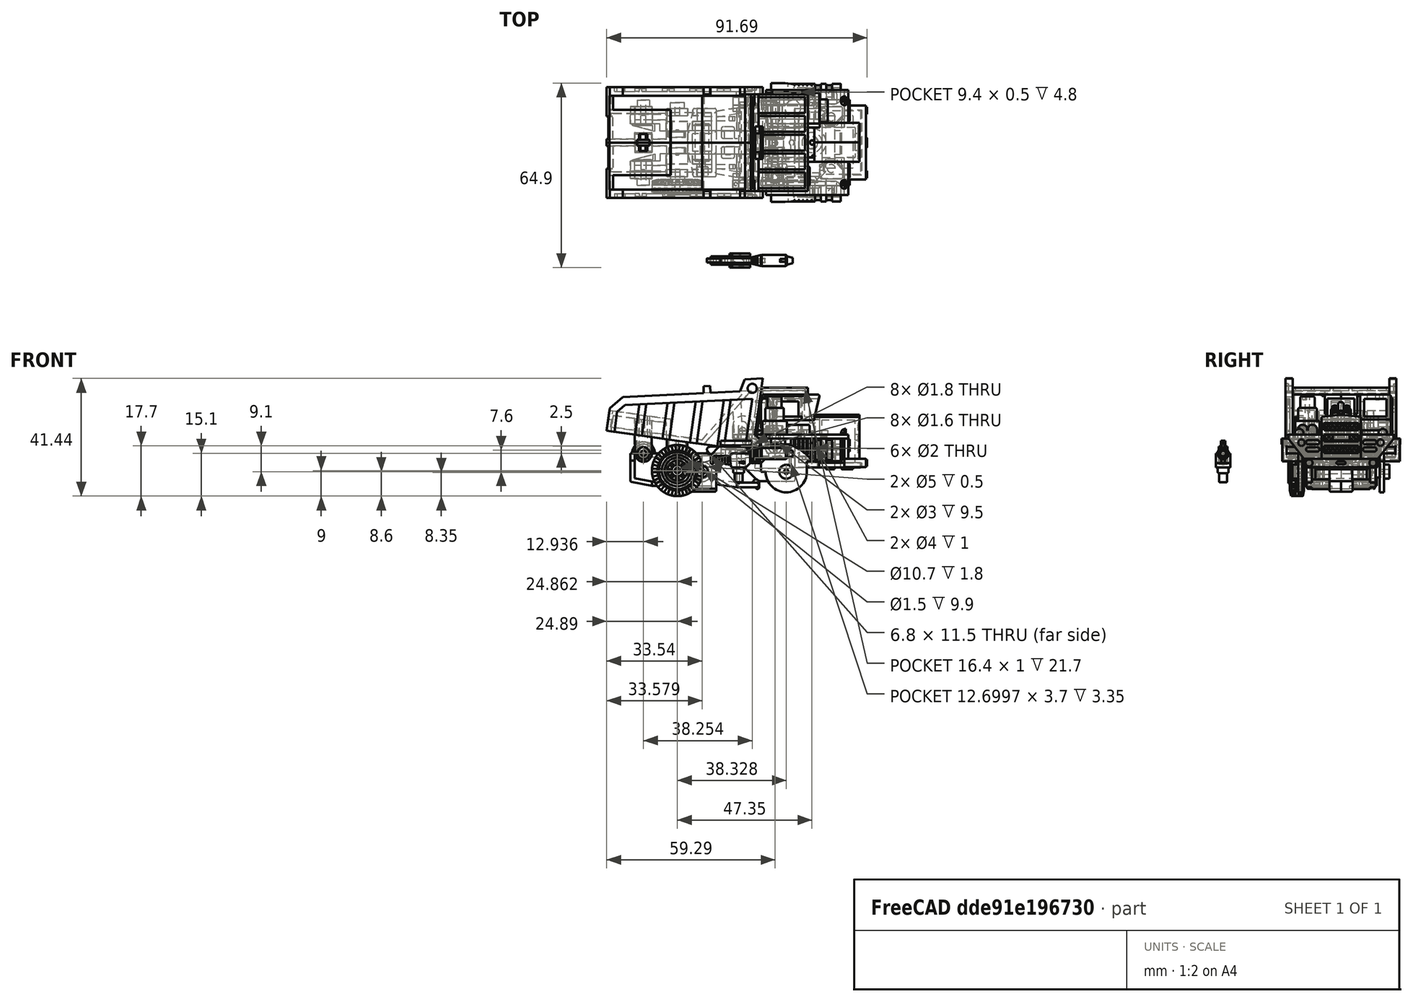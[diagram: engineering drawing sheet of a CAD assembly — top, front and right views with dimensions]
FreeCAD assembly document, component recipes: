
FREECAD ASSEMBLY — COMPONENT RECIPES ("Longhaul")

This assembly document has 21 components, labeled P0..P20 below (a component is one placed body or linked part). 19 of them carry a construction recipe — the FreeCAD feature program that regenerates the part from scratch, quoted from this document or its linked companion documents; the rest are supplied as boundary geometry only. No exploded tour is included for this assembly.
NOTE — this tour is split across 4 documents so each fits a 32k-token context. This is document 1: the component sections continue in the remaining 3 documents, each repeating the header above.
COMPONENT P0 — recipe-attached ("Lower_Torso", modeled in this document).
Construction recipe (the document's own serialized feature program — sketch geometry with constraints, then the solid features built on it; lengths are millimeters unless a unit is written):

FEATURE [Sketcher::SketchObject] Sketch
  ArcFitTolerance = 1e-06
  AttachmentSupport = -> [XY_Plane]
  FullyConstrained = true
  MakeInternals = false
  MapMode = 5
  sketch-geometry (8):
    g0: LineSegment StartX=0 StartY=11.25 StartZ=0 EndX=14.5 EndY=11.25 EndZ=0
    g1: LineSegment StartX=14.5 StartY=11.25 StartZ=0 EndX=14.5 EndY=-11.25 EndZ=0
    g2: LineSegment StartX=14.5 StartY=-11.25 StartZ=0 EndX=0 EndY=-11.25 EndZ=0
    g3: LineSegment StartX=0 StartY=-11.25 StartZ=0 EndX=0 EndY=-12 EndZ=0
    g4: LineSegment StartX=0 StartY=-12 StartZ=0 EndX=-8.5 EndY=-12 EndZ=0
    g5: LineSegment StartX=-8.5 StartY=-12 StartZ=0 EndX=-8.5 EndY=12 EndZ=0
    g6: LineSegment StartX=-8.5 StartY=12 StartZ=0 EndX=0 EndY=12 EndZ=0
    g7: LineSegment StartX=0 StartY=12 StartZ=0 EndX=0 EndY=11.25 EndZ=0
  constraints (26):
    c: Horizontal(g0)
    c: Coincident(g1,g0)
    c: Vertical(g1)
    c: Coincident(g2,g1)
    c: Horizontal(g2)
    c: Coincident(g3,g2)
    c: Vertical(g3)
    c: Coincident(g4,g3)
    c: Horizontal(g4)
    c: Coincident(g5,g4)
    c: Vertical(g5)
    c: Coincident(g6,g5)
    c: Horizontal(g6)
    c: Coincident(g7,g6)
    c: Coincident(g7,g0)
    c: Vertical(g7)
    c: DistanceY(g1,g1) = 22.5
    c: DistanceX(g0,g0) = 14.5
    c: DistanceX(g2,g2) = 14.5
    c: DistanceY(g3,g3) = 0.75
    c: DistanceY(g7,g7) = 0.75
    c: DistanceX(g6,g6) = 8.5
    c: DistanceY(g5,g5) = 24
    c: DistanceY(g-1,g5) = 12
    c: DistanceX(g5,g-1) = 8.5
    c: DistanceX(g5,g0) = 23
FEATURE [PartDesign::Pad] Pad
  Direction = (0,0,1)
  Length = 1.6
  Length2 = 10
  Profile = -> Sketch
  ReferenceAxis = -> Sketch [N_Axis]
  Refine = true
  Suppressed = false
  Type = 0
FEATURE [Sketcher::SketchObject] Sketch001
  ArcFitTolerance = 1e-06
  AttachmentSupport = -> [Pad]
  ExternalGeometry = -> [Pad]
  FullyConstrained = true
  MakeInternals = false
  MapMode = 5
  Placement = pos=(0,0,1.6) rot=(0,0,1;0rad)
  sketch-geometry (8):
    g0: LineSegment StartX=-8.5 StartY=12 StartZ=0 EndX=0 EndY=12 EndZ=0
    g1: LineSegment StartX=0 StartY=12 StartZ=0 EndX=0 EndY=10.6 EndZ=0
    g2: LineSegment StartX=0 StartY=10.6 StartZ=0 EndX=-7.1 EndY=10.6 EndZ=0
    g3: LineSegment StartX=-7.1 StartY=10.6 StartZ=0 EndX=-7.1 EndY=-10.6 EndZ=0
    g4: LineSegment StartX=-7.1 StartY=-10.6 StartZ=0 EndX=0 EndY=-10.6 EndZ=0
    g5: LineSegment StartX=0 StartY=-10.6 StartZ=0 EndX=0 EndY=-12 EndZ=0
    g6: LineSegment StartX=0 StartY=-12 StartZ=0 EndX=-8.5 EndY=-12 EndZ=0
    g7: LineSegment StartX=-8.5 StartY=-12 StartZ=0 EndX=-8.5 EndY=12 EndZ=0
  constraints (20):
    c: Coincident(g0,g-5)
    c: Coincident(g0,g-4)
    c: Coincident(g1,g0)
    c: PointOnObject(g1,g-2)
    c: Coincident(g2,g1)
    c: Horizontal(g2)
    c: Coincident(g3,g2)
    c: Vertical(g3)
    c: Coincident(g4,g3)
    c: PointOnObject(g4,g-2)
    c: Horizontal(g4)
    c: Coincident(g5,g4)
    c: Coincident(g5,g-7)
    c: Coincident(g6,g5)
    c: Coincident(g6,g-6)
    c: Coincident(g7,g6)
    c: Coincident(g7,g0)
    c: DistanceX(g6,g3) = 1.4
    c: DistanceY(g5,g4) = 1.4
    c: DistanceY(g2,g0) = 1.4
FEATURE [PartDesign::Pad] Pad001
  BaseFeature = -> Pad
  Direction = (0,0,1)
  Length = 8.5
  Length2 = 10
  Profile = -> Sketch001
  ReferenceAxis = -> Sketch001 [N_Axis]
  Refine = true
  Suppressed = false
  Type = 0
FEATURE [Sketcher::SketchObject] Sketch002
  ArcFitTolerance = 1e-06
  AttachmentSupport = -> [Pad001]
  ExternalGeometry = -> [Pad001]
  FullyConstrained = true
  MakeInternals = false
  MapMode = 5
  Placement = pos=(0,0,1.6) rot=(0,0,1;0rad)
  sketch-geometry (4):
    g0: LineSegment StartX=5.4 StartY=4.1 StartZ=0 EndX=5.4 EndY=-4.1 EndZ=0
    g1: LineSegment StartX=5.4 StartY=-4.1 StartZ=0 EndX=7.5 EndY=-4.1 EndZ=0
    g2: LineSegment StartX=7.5 StartY=-4.1 StartZ=0 EndX=7.5 EndY=4.1 EndZ=0
    g3: LineSegment StartX=7.5 StartY=4.1 StartZ=0 EndX=5.4 EndY=4.1 EndZ=0
  constraints (13):
    c: Coincident(g0,g1)
    c: Coincident(g1,g2)
    c: Coincident(g2,g3)
    c: Coincident(g3,g0)
    c: Vertical(g0)
    c: Vertical(g2)
    c: Horizontal(g1)
    c: Horizontal(g3)
    c: DistanceY(g2,g2) = 8.2
    c: DistanceX(g3,g3) = 2.1
    c: DistanceY(g-3,g-3) = 22.5
    c: DistanceY(g2,g-3) = 7.15
    c: DistanceX(g1,g-3) = 7
FEATURE [PartDesign::Pocket] Pocket
  BaseFeature = -> Pad001
  Direction = (0,0,-1)
  Length = 5
  Length2 = 5
  Profile = -> Sketch002
  ReferenceAxis = -> Sketch002 [N_Axis]
  Refine = true
  Suppressed = false
  Type = 0
FEATURE [Sketcher::SketchObject] Sketch003
  ArcFitTolerance = 1e-06
  AttachmentSupport = -> [Pocket]
  ExternalGeometry = -> [Pocket]
  FullyConstrained = true
  MakeInternals = false
  MapMode = 5
  Placement = pos=(0,0,10.1) rot=(0,0,1;0rad)
  sketch-geometry (4):
    g0: LineSegment StartX=-8.5 StartY=2.5 StartZ=0 EndX=-8.5 EndY=-2.5 EndZ=0
    g1: LineSegment StartX=-8.5 StartY=-2.5 StartZ=0 EndX=-7.1 EndY=-2.5 EndZ=0
    g2: LineSegment StartX=-7.1 StartY=-2.5 StartZ=0 EndX=-7.1 EndY=2.5 EndZ=0
    g3: LineSegment StartX=-7.1 StartY=2.5 StartZ=0 EndX=-8.5 EndY=2.5 EndZ=0
  constraints (12):
    c: Coincident(g0,g1)
    c: Coincident(g1,g2)
    c: Coincident(g2,g3)
    c: Coincident(g3,g0)
    c: Vertical(g0)
    c: Vertical(g2)
    c: Horizontal(g1)
    c: Horizontal(g3)
    c: PointOnObject(g0,g-4)
    c: PointOnObject(g1,g-3)
    c: DistanceY(g0,g0) = 5
    c: DistanceY(g1,g-1) = 2.5
FEATURE [PartDesign::Pocket] Pocket001
  BaseFeature = -> Pocket
  Direction = (0,0,-1)
  Length = 5
  Length2 = 5
  Profile = -> Sketch003
  ReferenceAxis = -> Sketch003 [N_Axis]
  Refine = true
  Suppressed = false
  Type = 0
FEATURE [Sketcher::SketchObject] Sketch004
  ArcFitTolerance = 1e-06
  AttachmentSupport = -> [Pocket001]
  ExternalGeometry = -> [Pocket001]
  FullyConstrained = true
  MakeInternals = false
  MapMode = 5
  Placement = pos=(0,0,10.1) rot=(0,0,1;0rad)
  sketch-geometry (4):
    g0: ArcOfCircle CenterX=-0.7 CenterY=-12 CenterZ=0 NormalX=0 NormalY=0 NormalZ=1 AngleXU=0 Radius=0.7 StartAngle=3.14159 EndAngle=6.28319
    g1: ArcOfCircle CenterX=-0.7 CenterY=12 CenterZ=0 NormalX=0 NormalY=0 NormalZ=1 AngleXU=0 Radius=0.7 StartAngle=-9e-16 EndAngle=3.14159
    g2: LineSegment StartX=0 StartY=-12 StartZ=0 EndX=-1.4 EndY=-12 EndZ=0
    g3: LineSegment StartX=0 StartY=12 StartZ=0 EndX=-1.4 EndY=12 EndZ=0
  constraints (13):
    c: Coincident(g0,g-3)
    c: PointOnObject(g0,g-3)
    c: Coincident(g1,g-4)
    c: PointOnObject(g1,g-4)
    c: PointOnObject(g0,g-3)
    c: PointOnObject(g1,g-4)
    c: DistanceY(g-5,g-5) = 1.4
    c: Radius(g1) = 0.7
    c: Radius(g0) = 0.7
    c: Coincident(g2,g0)
    c: Coincident(g2,g0)
    c: Coincident(g3,g1)
    c: Coincident(g3,g1)
FEATURE [PartDesign::Pad] Pad002
  BaseFeature = -> Pocket001
  Direction = (0,0,1)
  Length = 10
  Length2 = 10
  Profile = -> Sketch004
  ReferenceAxis = -> Sketch004 [N_Axis]
  Refine = true
  Reversed = true
  Suppressed = false
  Type = 0
FEATURE [Sketcher::SketchObject] Sketch005
  ArcFitTolerance = 1e-06
  AttachmentSupport = -> [Pad002]
  ExternalGeometry = -> [Pad002]
  FullyConstrained = true
  MakeInternals = false
  MapMode = 5
  Placement = pos=(0,-12,0) rot=(1,0,0;1.5708rad)
  sketch-geometry (8):
    g0: LineSegment StartX=0 StartY=10.1 StartZ=0 EndX=-2 EndY=10.1 EndZ=0
    g1: LineSegment StartX=-2 StartY=10.1 StartZ=0 EndX=-2 EndY=8.1 EndZ=0
    g2: LineSegment StartX=-2 StartY=8.1 StartZ=0 EndX=0 EndY=8.1 EndZ=0
    g3: LineSegment StartX=0 StartY=8.1 StartZ=0 EndX=0 EndY=10.1 EndZ=0
    g4: LineSegment StartX=0 StartY=0 StartZ=0 EndX=0 EndY=2 EndZ=0
    g5: LineSegment StartX=0 StartY=2 StartZ=0 EndX=-2 EndY=2 EndZ=0
    g6: LineSegment StartX=-2 StartY=2 StartZ=0 EndX=-2 EndY=0 EndZ=0
    g7: LineSegment StartX=-2 StartY=0 StartZ=0 EndX=0 EndY=0 EndZ=0
  constraints (22):
    c: Coincident(g0,g1)
    c: Coincident(g1,g2)
    c: Coincident(g2,g3)
    c: Coincident(g3,g0)
    c: Horizontal(g0)
    c: Horizontal(g2)
    c: Vertical(g1)
    c: Vertical(g3)
    c: Coincident(g0,g-5)
    c: Coincident(g4,g5)
    c: Coincident(g5,g6)
    c: Coincident(g6,g7)
    c: Coincident(g7,g4)
    c: Vertical(g4)
    c: Vertical(g6)
    c: Horizontal(g5)
    c: Horizontal(g7)
    c: Coincident(g4,g-1)
    c: DistanceY(g6,g6) = 2
    c: DistanceY(g1,g1) = 2
    c: DistanceX(g0,g0) = 2
    c: DistanceX(g5,g5) = 2
FEATURE [PartDesign::Pocket] Pocket002
  BaseFeature = -> Pad002
  Direction = (0,1,-2e-16)
  Length = 5
  Length2 = 5
  Profile = -> Sketch005
  ReferenceAxis = -> Sketch005 [N_Axis]
  Refine = true
  Reversed = true
  Suppressed = false
  Type = 0
FEATURE [Sketcher::SketchObject] Sketch006
  ArcFitTolerance = 1e-06
  AttachmentSupport = -> [Pocket002]
  ExternalGeometry = -> [Pocket002]
  FullyConstrained = true
  MakeInternals = false
  MapMode = 5
  Placement = pos=(0,12,0) rot=(0,0.707107,0.707107;3.14159rad)
  sketch-geometry (8):
    g0: LineSegment StartX=0 StartY=10.1 StartZ=0 EndX=0 EndY=8.1 EndZ=0
    g1: LineSegment StartX=0 StartY=8.1 StartZ=0 EndX=2 EndY=8.1 EndZ=0
    g2: LineSegment StartX=2 StartY=8.1 StartZ=0 EndX=2 EndY=10.1 EndZ=0
    g3: LineSegment StartX=2 StartY=10.1 StartZ=0 EndX=0 EndY=10.1 EndZ=0
    g4: LineSegment StartX=0 StartY=0 StartZ=0 EndX=2 EndY=0 EndZ=0
    g5: LineSegment StartX=2 StartY=0 StartZ=0 EndX=2 EndY=2 EndZ=0
    g6: LineSegment StartX=2 StartY=2 StartZ=0 EndX=0 EndY=2 EndZ=0
    g7: LineSegment StartX=0 StartY=2 StartZ=0 EndX=0 EndY=0 EndZ=0
  constraints (22):
    c: Coincident(g0,g1)
    c: Coincident(g1,g2)
    c: Coincident(g2,g3)
    c: Coincident(g3,g0)
    c: Vertical(g0)
    c: Vertical(g2)
    c: Horizontal(g1)
    c: Horizontal(g3)
    c: Coincident(g0,g-3)
    c: Coincident(g4,g5)
    c: Coincident(g5,g6)
    c: Coincident(g6,g7)
    c: Coincident(g7,g4)
    c: Horizontal(g4)
    c: Horizontal(g6)
    c: Vertical(g5)
    c: Vertical(g7)
    c: Coincident(g4,g-1)
    c: DistanceX(g6,g6) = 2
    c: DistanceX(g1,g1) = 2
    c: DistanceY(g2,g2) = 2
    c: DistanceY(g5,g5) = 2
FEATURE [PartDesign::Pocket] Pocket003
  BaseFeature = -> Pocket002
  Direction = (0,-1,2e-16)
  Length = 5
  Length2 = 5
  Profile = -> Sketch006
  ReferenceAxis = -> Sketch006 [N_Axis]
  Refine = true
  Reversed = true
  Suppressed = false
  Type = 0
FEATURE [Sketcher::SketchObject] Sketch007
  ArcFitTolerance = 1e-06
  AttachmentSupport = -> [Pocket003]
  ExternalGeometry = -> [Pocket003]
  FullyConstrained = true
  MakeInternals = false
  MapMode = 5
  Placement = pos=(0,0,0) rot=(1,0,0;3.14159rad)
  sketch-geometry (1):
    g0: Circle CenterX=-2.5 CenterY=0 CenterZ=0 NormalX=0 NormalY=0 NormalZ=1 AngleXU=0 Radius=1
  constraints (4):
    c: PointOnObject(g0,g-1)
    c: Radius(g0) = 1
    c: DistanceX(g0,g-3) = 17
    c: DistanceX(g-4,g0) = 6
FEATURE [PartDesign::Pocket] Pocket004
  BaseFeature = -> Pocket003
  Direction = (0,0,1)
  Length = 5
  Length2 = 5
  Profile = -> Sketch007
  ReferenceAxis = -> Sketch007 [N_Axis]
  Refine = true
  Suppressed = false
  Type = 0
FEATURE [Sketcher::SketchObject] Sketch008
  ArcFitTolerance = 1e-06
  AttachmentSupport = -> [Pocket004]
  ExternalGeometry = -> [Pocket004]
  FullyConstrained = false
  MakeInternals = false
  MapMode = 5
  Placement = pos=(0,0,1.6) rot=(0,0,1;0rad)
  sketch-geometry (1):
    g0: Circle CenterX=-2.5 CenterY=0 CenterZ=0 NormalX=0 NormalY=0 NormalZ=1 AngleXU=0 Radius=4.9
  constraints (1):
    c: Radius(g0) = 4.9
FEATURE [PartDesign::Pad] Pad003
  BaseFeature = -> Pocket004
  Direction = (0,0,1)
  Length = 1.2
  Length2 = 10
  Profile = -> Sketch008
  ReferenceAxis = -> Sketch008 [N_Axis]
  Refine = true
  Suppressed = false
  Type = 0
FEATURE [Sketcher::SketchObject] Sketch009
  ArcFitTolerance = 1e-06
  AttachmentSupport = -> [Pad003]
  ExternalGeometry = -> [Pad003]
  FullyConstrained = true
  MakeInternals = false
  MapMode = 5
  Placement = pos=(0,0,2.8) rot=(0,0,1;0rad)
  sketch-geometry (1):
    g0: Circle CenterX=-2.5 CenterY=0 CenterZ=0 NormalX=0 NormalY=0 NormalZ=1 AngleXU=0 Radius=3.55
  constraints (2):
    c: Coincident(g0,g-3)
    c: Radius(g0) = 3.55
FEATURE [PartDesign::Pad] Pad004
  BaseFeature = -> Pad003
  Direction = (0,0,1)
  Length = 1
  Length2 = 10
  Profile = -> Sketch009
  ReferenceAxis = -> Sketch009 [N_Axis]
  Refine = true
  Suppressed = false
  Type = 0
FEATURE [Sketcher::SketchObject] Sketch010
  ArcFitTolerance = 1e-06
  AttachmentSupport = -> [Pad004]
  ExternalGeometry = -> [Pad004]
  FullyConstrained = true
  MakeInternals = false
  MapMode = 5
  Placement = pos=(0,0,3.8) rot=(0,0,1;0rad)
  sketch-geometry (1):
    g0: Circle CenterX=-2.5 CenterY=0 CenterZ=0 NormalX=0 NormalY=0 NormalZ=1 AngleXU=0 Radius=2.25
  constraints (2):
    c: Coincident(g0,g-3)
    c: Diameter(g0) = 4.5
FEATURE [PartDesign::Pocket] Pocket005
  BaseFeature = -> Pad004
  Direction = (0,0,-1)
  Length = 1
  Length2 = 5
  Profile = -> Sketch010
  ReferenceAxis = -> Sketch010 [N_Axis]
  Refine = true
  Suppressed = false
  Type = 0
FEATURE [Sketcher::SketchObject] Sketch011
  ArcFitTolerance = 1e-06
  AttachmentSupport = -> [Pocket005]
  ExternalGeometry = -> [Pocket005]
  FullyConstrained = true
  MakeInternals = false
  MapMode = 5
  Placement = pos=(0,0,2.8) rot=(0,0,1;0rad)
  sketch-geometry (1):
    g0: Circle CenterX=-2.5 CenterY=0 CenterZ=0 NormalX=0 NormalY=0 NormalZ=1 AngleXU=0 Radius=1
  constraints (2):
    c: Coincident(g0,g-3)
    c: Radius(g0) = 1
FEATURE [PartDesign::Pocket] Pocket006
  BaseFeature = -> Pocket005
  Direction = (0,0,-1)
  Length = 1.2
  Length2 = 5
  Profile = -> Sketch011
  ReferenceAxis = -> Sketch011 [N_Axis]
  Refine = true
  Suppressed = false
  Type = 0
FEATURE [Sketcher::SketchObject] Sketch012
  ArcFitTolerance = 1e-06
  AttachmentSupport = -> [Pocket006]
  ExternalGeometry = -> [Sketch007]
  FullyConstrained = true
  MakeInternals = false
  MapMode = 5
  Placement = pos=(0,0,0) rot=(1,0,0;3.14159rad)
  sketch-geometry (1):
    g0: Circle CenterX=-2.5 CenterY=0 CenterZ=0 NormalX=0 NormalY=0 NormalZ=1 AngleXU=0 Radius=2
  constraints (2):
    c: Coincident(g0,g-3)
    c: Diameter(g0) = 4
FEATURE [PartDesign::Pocket] Pocket007
  BaseFeature = -> Pocket006
  Direction = (0,0,1)
  Length = 1.8
  Length2 = 5
  Profile = -> Sketch012
  ReferenceAxis = -> Sketch012 [N_Axis]
  Refine = true
  Suppressed = false
  Type = 0
FEATURE [Sketcher::SketchObject] Sketch013
  ArcFitTolerance = 1e-06
  AttachmentSupport = -> [Pocket007]
  ExternalGeometry = -> [Pocket007]
  FullyConstrained = true
  MakeInternals = false
  MapMode = 5
  Placement = pos=(0,0,0) rot=(1,0,0;3.14159rad)
  sketch-geometry (24):
    g0: LineSegment StartX=11.65 StartY=9 StartZ=0 EndX=8.15 EndY=9 EndZ=0
    g1: LineSegment StartX=7.9 StartY=8.75 StartZ=0 EndX=7.9 EndY=-9.25 EndZ=0
    g2: LineSegment StartX=8.15 StartY=-9.5 StartZ=0 EndX=11.65 EndY=-9.5 EndZ=0
    g3: LineSegment StartX=11.9 StartY=-9.25 StartZ=0 EndX=11.9 EndY=8.75 EndZ=0
    g4: LineSegment StartX=2.4 StartY=8.75 StartZ=0 EndX=2.4 EndY=-9.25 EndZ=0
    g5: LineSegment StartX=2.65 StartY=-9.5 StartZ=0 EndX=5.15 EndY=-9.5 EndZ=0
    g6: LineSegment StartX=5.4 StartY=-9.25 StartZ=0 EndX=5.4 EndY=8.75 EndZ=0
    g7: LineSegment StartX=5.15 StartY=9 StartZ=0 EndX=2.65 EndY=9 EndZ=0
    g8: ArcOfCircle CenterX=11.65 CenterY=8.75 CenterZ=0 NormalX=0 NormalY=0 NormalZ=1 AngleXU=0 Radius=0.25 StartAngle=2.7e-15 EndAngle=1.5708
    g9: GeomPoint [constr] X=11.9 Y=9 Z=0
    g10: ArcOfCircle CenterX=8.15 CenterY=8.75 CenterZ=0 NormalX=0 NormalY=0 NormalZ=1 AngleXU=0 Radius=0.25 StartAngle=1.5708 EndAngle=3.14159
    g11: GeomPoint [constr] X=7.9 Y=9 Z=0
    g12: ArcOfCircle CenterX=8.15 CenterY=-9.25 CenterZ=0 NormalX=0 NormalY=0 NormalZ=1 AngleXU=0 Radius=0.25 StartAngle=3.14159 EndAngle=4.71239
    g13: GeomPoint [constr] X=7.9 Y=-9.5 Z=0
    g14: ArcOfCircle CenterX=11.65 CenterY=-9.25 CenterZ=0 NormalX=0 NormalY=0 NormalZ=1 AngleXU=0 Radius=0.25 StartAngle=4.71239 EndAngle=6.28319
    g15: GeomPoint [constr] X=11.9 Y=-9.5 Z=0
    g16: ArcOfCircle CenterX=5.15 CenterY=-9.25 CenterZ=0 NormalX=0 NormalY=0 NormalZ=1 AngleXU=0 Radius=0.25 StartAngle=4.71239 EndAngle=6.28319
    g17: GeomPoint [constr] X=5.4 Y=-9.5 Z=0
    g18: ArcOfCircle CenterX=2.65 CenterY=-9.25 CenterZ=0 NormalX=0 NormalY=0 NormalZ=1 AngleXU=0 Radius=0.25 StartAngle=3.14159 EndAngle=4.71239
    g19: GeomPoint [constr] X=2.4 Y=-9.5 Z=0
    g20: ArcOfCircle CenterX=2.65 CenterY=8.75 CenterZ=0 NormalX=0 NormalY=0 NormalZ=1 AngleXU=0 Radius=0.25 StartAngle=1.5708 EndAngle=3.14159
    g21: GeomPoint [constr] X=2.4 Y=9 Z=0
    g22: ArcOfCircle CenterX=5.15 CenterY=8.75 CenterZ=0 NormalX=0 NormalY=0 NormalZ=1 AngleXU=0 Radius=0.25 StartAngle=2.9e-15 EndAngle=1.5708
    g23: GeomPoint [constr] X=5.4 Y=9 Z=0
  constraints (57):
    c: Horizontal(g0)
    c: Horizontal(g2)
    c: Vertical(g1)
    c: Vertical(g3)
    c: Vertical(g4)
    c: Vertical(g6)
    c: Horizontal(g5)
    c: Horizontal(g7)
    c: PointOnObject(g9,g0)
    c: PointOnObject(g9,g3)
    c: Tangent(g0,g8) = -1.5708
    c: Tangent(g3,g8) = -1.5708
    c: PointOnObject(g11,g0)
    c: PointOnObject(g11,g1)
    c: Tangent(g0,g10) = -1.5708
    c: Tangent(g1,g10) = -1.5708
    c: PointOnObject(g13,g1)
    c: PointOnObject(g13,g2)
    c: Tangent(g1,g12) = -1.5708
    c: Tangent(g2,g12) = -1.5708
    c: PointOnObject(g15,g2)
    c: PointOnObject(g15,g3)
    c: Tangent(g2,g14) = -1.5708
    c: Tangent(g3,g14) = -1.5708
    c: PointOnObject(g17,g5)
    c: PointOnObject(g17,g6)
    c: Tangent(g5,g16) = -1.5708
    c: Tangent(g6,g16) = -1.5708
    c: PointOnObject(g19,g4)
    c: PointOnObject(g19,g5)
    c: Tangent(g4,g18) = -1.5708
    c: Tangent(g5,g18) = -1.5708
    c: PointOnObject(g21,g4)
    c: PointOnObject(g21,g7)
    c: Tangent(g4,g20) = -1.5708
    c: Tangent(g7,g20) = -1.5708
    c: PointOnObject(g23,g6)
    c: PointOnObject(g23,g7)
    c: Tangent(g6,g22) = -1.5708
    c: Tangent(g7,g22) = -1.5708
    c: Radius(g20) = 0.25
    c: Radius(g22) = 0.25
    c: Radius(g18) = 0.25
    c: Radius(g16) = 0.25
    c: Radius(g12) = 0.25
    c: Radius(g14) = 0.25
    c: Radius(g10) = 0.25
    c: Radius(g8) = 0.25
    c: PointOnObject(g-3,g6)
    c: DistanceY(g3,g3) = 18
    c: DistanceY(g4,g4) = 18
    c: DistanceY(g-4,g-4) = 22.5
    c: DistanceY(g0,g-4) = 2.25
    c: DistanceY(g7,g-5) = 2.25
    c: DistanceX(g1,g3) = 4
    c: DistanceX(g4,g6) = 3
    c: DistanceX(g3,g-5) = 2.6
FEATURE [PartDesign::Pad] Pad005
  BaseFeature = -> Pocket007
  Direction = (0,0,-1)
  Length = 0.6
  Length2 = 10
  Profile = -> Sketch013
  ReferenceAxis = -> Sketch013 [N_Axis]
  Refine = true
  Suppressed = false
  Type = 0
FEATURE [Sketcher::SketchObject] Sketch014
  ArcFitTolerance = 1e-06
  AttachmentSupport = -> [Pad005]
  ExternalGeometry = -> [Pad005]
  FullyConstrained = true
  MakeInternals = false
  MapMode = 5
  Placement = pos=(-8.5,0,0) rot=(0.57735,-0.57735,-0.57735;2.0944rad)
  sketch-geometry (8):
    g0: LineSegment StartX=4 StartY=10.1 StartZ=0 EndX=4 EndY=3.4 EndZ=0
    g1: LineSegment StartX=4 StartY=3.4 StartZ=0 EndX=-4 EndY=3.4 EndZ=0
    g2: LineSegment StartX=-4 StartY=3.4 StartZ=0 EndX=-4 EndY=10.1 EndZ=0
    g3: LineSegment StartX=-4 StartY=10.1 StartZ=0 EndX=-2.5 EndY=10.1 EndZ=0
    g4: LineSegment StartX=2.5 StartY=10.1 StartZ=0 EndX=4 EndY=10.1 EndZ=0
    g5: LineSegment StartX=-2.5 StartY=10.1 StartZ=0 EndX=-2.5 EndY=5.1 EndZ=0
    g6: LineSegment StartX=-2.5 StartY=5.1 StartZ=0 EndX=2.5 EndY=5.1 EndZ=0
    g7: LineSegment StartX=2.5 StartY=5.1 StartZ=0 EndX=2.5 EndY=10.1 EndZ=0
  constraints (20):
    c: PointOnObject(g0,g-3)
    c: Vertical(g0)
    c: Coincident(g1,g0)
    c: Horizontal(g1)
    c: Coincident(g2,g1)
    c: PointOnObject(g2,g-7)
    c: Vertical(g2)
    c: Coincident(g3,g2)
    c: Coincident(g3,g-7)
    c: Coincident(g0,g4)
    c: Coincident(g5,g3)
    c: Coincident(g5,g-6)
    c: Coincident(g6,g5)
    c: Coincident(g6,g-5)
    c: Coincident(g7,g6)
    c: Coincident(g7,g4)
    c: DistanceX(g3,g3) = 1.5
    c: DistanceX(g4,g4) = 1.5
    c: DistanceY(g-8,g0) = 3.4
    c: Coincident(g4,g-4)
FEATURE [PartDesign::Pad] Pad006
  BaseFeature = -> Pad005
  Direction = (-1,0,0)
  Length = 17.6
  Length2 = 10
  Profile = -> Sketch014
  ReferenceAxis = -> Sketch014 [N_Axis]
  Refine = true
  Suppressed = false
  Type = 0
FEATURE [Sketcher::SketchObject] Sketch015
  ArcFitTolerance = 1e-06
  AttachmentSupport = -> [Pad006]
  ExternalGeometry = -> [Pad006]
  FullyConstrained = true
  MakeInternals = false
  MapMode = 5
  Placement = pos=(0,4,0) rot=(0,0.707107,0.707107;3.14159rad)
  sketch-geometry (8):
    g0: LineSegment StartX=11.9 StartY=10.1 StartZ=0 EndX=12.9 EndY=10.1 EndZ=0
    g1: LineSegment StartX=18.1 StartY=10.1 StartZ=0 EndX=19.1 EndY=10.1 EndZ=0
    g2: ArcOfCircle CenterX=15.5 CenterY=7.5 CenterZ=0 NormalX=0 NormalY=0 NormalZ=1 AngleXU=0 Radius=3.6 StartAngle=3.14159 EndAngle=6.28319
    g3: LineSegment StartX=11.9 StartY=10.1 StartZ=0 EndX=11.9 EndY=7.5 EndZ=0
    g4: LineSegment StartX=19.1 StartY=7.5 StartZ=0 EndX=19.1 EndY=10.1 EndZ=0
    g5: ArcOfCircle CenterX=15.5 CenterY=7.5 CenterZ=0 NormalX=0 NormalY=0 NormalZ=1 AngleXU=0 Radius=2.6 StartAngle=3.14159 EndAngle=6.28319
    g6: LineSegment StartX=18.1 StartY=7.5 StartZ=0 EndX=18.1 EndY=10.1 EndZ=0
    g7: LineSegment StartX=12.9 StartY=7.5 StartZ=0 EndX=12.9 EndY=10.1 EndZ=0
  constraints (25):
    c: PointOnObject(g0,g-4)
    c: PointOnObject(g0,g-4)
    c: PointOnObject(g1,g-4)
    c: DistanceX(g-4,g0) = 3.4
    c: DistanceX(g0,g0) = 1
    c: DistanceX(g1,g1) = 1
    c: DistanceX(g0,g1) = 5.2
    c: Diameter(g2) = 7.2
    c: Coincident(g3,g0)
    c: Coincident(g3,g2)
    c: Coincident(g4,g2)
    c: Coincident(g4,g1)
    c: Vertical(g4)
    c: Vertical(g3)
    c: DistanceY(g2,g2) = 0
    c: PointOnObject(g1,g-4)
    c: Diameter(g5) = 5.2
    c: Coincident(g6,g5)
    c: Coincident(g6,g1)
    c: Vertical(g6)
    c: Coincident(g7,g5)
    c: Coincident(g7,g0)
    c: Vertical(g7)
    c: Coincident(g5,g2)
    c: DistanceY(g-5,g2) = 4.1
FEATURE [PartDesign::Pad] Pad007
  BaseFeature = -> Pad006
  Direction = (0,1,-2e-16)
  Length = 9
  Length2 = 10
  Profile = -> Sketch015
  ReferenceAxis = -> Sketch015 [N_Axis]
  Refine = true
  Suppressed = false
  Type = 0
FEATURE [Sketcher::SketchObject] Sketch016
  ArcFitTolerance = 1e-06
  AttachmentSupport = -> [Pad007]
  ExternalGeometry = -> [Pad007]
  FullyConstrained = true
  MakeInternals = false
  MapMode = 5
  Placement = pos=(0,-4,0) rot=(1,0,0;1.5708rad)
  sketch-geometry (8):
    g0: LineSegment StartX=-11.9 StartY=10.1 StartZ=0 EndX=-12.9 EndY=10.1 EndZ=0
    g1: LineSegment StartX=-18.1 StartY=10.1 StartZ=0 EndX=-19.1 EndY=10.1 EndZ=0
    g2: ArcOfCircle CenterX=-15.5 CenterY=7.5 CenterZ=0 NormalX=0 NormalY=0 NormalZ=1 AngleXU=0 Radius=3.6 StartAngle=3.14159 EndAngle=6.28319
    g3: LineSegment StartX=-11.9 StartY=10.1 StartZ=0 EndX=-11.9 EndY=7.5 EndZ=0
    g4: LineSegment StartX=-19.1 StartY=10.1 StartZ=0 EndX=-19.1 EndY=7.5 EndZ=0
    g5: ArcOfCircle CenterX=-15.5 CenterY=7.5 CenterZ=0 NormalX=0 NormalY=0 NormalZ=1 AngleXU=0 Radius=2.6 StartAngle=3.14159 EndAngle=6.28319
    g6: LineSegment StartX=-18.1 StartY=10.1 StartZ=0 EndX=-18.1 EndY=7.5 EndZ=0
    g7: LineSegment StartX=-12.9 StartY=10.1 StartZ=0 EndX=-12.9 EndY=7.5 EndZ=0
  constraints (25):
    c: PointOnObject(g0,g-3)
    c: PointOnObject(g0,g-3)
    c: PointOnObject(g1,g-3)
    c: PointOnObject(g1,g-3)
    c: DistanceX(g0,g-3) = 3.4
    c: DistanceX(g0,g0) = 1
    c: DistanceX(g1,g1) = 1
    c: DistanceX(g1,g0) = 5.2
    c: Diameter(g2) = 7.2
    c: Coincident(g3,g0)
    c: Coincident(g3,g2)
    c: Coincident(g4,g1)
    c: Coincident(g4,g2)
    c: Vertical(g4)
    c: Vertical(g3)
    c: Coincident(g6,g1)
    c: Coincident(g6,g5)
    c: Vertical(g6)
    c: Coincident(g7,g0)
    c: Coincident(g7,g5)
    c: Coincident(g2,g5)
    c: Diameter(g5) = 5.2
    c: DistanceY(g-4,g2) = 4.1
    c: Vertical(g7)
    c: DistanceY(g5,g2) = 0
FEATURE [PartDesign::Pad] Pad008
  BaseFeature = -> Pad007
  Direction = (0,-1,2e-16)
  Length = 9
  Length2 = 10
  Profile = -> Sketch016
  ReferenceAxis = -> Sketch016 [N_Axis]
  Refine = true
  Suppressed = false
  Type = 0
FEATURE [Sketcher::SketchObject] Sketch017
  ArcFitTolerance = 1e-06
  AttachmentSupport = -> [Pad008]
  ExternalGeometry = -> [Pad008]
  FullyConstrained = false
  MakeInternals = false
  MapMode = 5
  Placement = pos=(0,4,0) rot=(0,0.707107,0.707107;3.14159rad)
  sketch-geometry (4):
    g0: LineSegment StartX=12.9 StartY=10.1 StartZ=0 EndX=12.9 EndY=7.5 EndZ=0
    g1: LineSegment StartX=12.9 StartY=10.1 StartZ=0 EndX=18.1 EndY=10.1 EndZ=0
    g2: LineSegment StartX=18.1 StartY=10.1 StartZ=0 EndX=18.1 EndY=7.5 EndZ=0
    g3: ArcOfCircle CenterX=15.5 CenterY=7.5 CenterZ=0 NormalX=0 NormalY=0 NormalZ=1 AngleXU=0 Radius=2.6 StartAngle=3.14159 EndAngle=6.28319
  constraints (8):
    c: Coincident(g0,g-3)
    c: Coincident(g0,g-4)
    c: Coincident(g1,g0)
    c: Coincident(g1,g-3)
    c: Coincident(g2,g1)
    c: Coincident(g2,g-4)
    c: Coincident(g3,g2)
    c: Coincident(g3,g0)
FEATURE [PartDesign::Pocket] Pocket008
  BaseFeature = -> Pad008
  Direction = (0,-1,2e-16)
  Length = 1.5
  Length2 = 5
  Profile = -> Sketch017
  ReferenceAxis = -> Sketch017 [N_Axis]
  Refine = true
  Suppressed = false
  Type = 0
FEATURE [Sketcher::SketchObject] Sketch018
  ArcFitTolerance = 1e-06
  AttachmentSupport = -> [Pocket008]
  ExternalGeometry = -> [Pocket008]
  FullyConstrained = true
  MakeInternals = false
  MapMode = 5
  Placement = pos=(0,-4,0) rot=(1,0,0;1.5708rad)
  sketch-geometry (4):
    g0: LineSegment StartX=-18.1 StartY=7.5 StartZ=0 EndX=-18.1 EndY=10.1 EndZ=0
    g1: LineSegment StartX=-18.1 StartY=10.1 StartZ=0 EndX=-12.9 EndY=10.1 EndZ=0
    g2: LineSegment StartX=-12.9 StartY=10.1 StartZ=0 EndX=-12.9 EndY=7.5 EndZ=0
    g3: ArcOfCircle CenterX=-15.5 CenterY=7.5 CenterZ=0 NormalX=0 NormalY=0 NormalZ=1 AngleXU=0 Radius=2.6 StartAngle=3.14159 EndAngle=6.28319
  constraints (8):
    c: Coincident(g0,g-5)
    c: Coincident(g0,g-4)
    c: Coincident(g1,g0)
    c: Coincident(g1,g-3)
    c: Coincident(g2,g1)
    c: Coincident(g2,g-5)
    c: Coincident(g3,g2)
    c: Tangent(g3,g-5) = -1.5708
FEATURE [PartDesign::Pocket] Pocket009
  BaseFeature = -> Pocket008
  Direction = (0,1,-2e-16)
  Length = 1.5
  Length2 = 5
  Profile = -> Sketch018
  ReferenceAxis = -> Sketch018 [N_Axis]
  Refine = true
  Suppressed = false
  Type = 0
FEATURE [Sketcher::SketchObject] Sketch019
  ArcFitTolerance = 1e-06
  AttachmentSupport = -> [Pocket009]
  ExternalGeometry = -> [Pocket009]
  FullyConstrained = true
  MakeInternals = false
  MapMode = 5
  Placement = pos=(0,2.5,0) rot=(1,0,0;1.5708rad)
  sketch-geometry (8):
    g0: LineSegment StartX=-18.75 StartY=10.1 StartZ=0 EndX=-17 EndY=10.1 EndZ=0
    g1: LineSegment StartX=-12.25 StartY=10.1 StartZ=0 EndX=-14 EndY=10.1 EndZ=0
    g2: LineSegment StartX=-14 StartY=10.1 StartZ=0 EndX=-14 EndY=6.9 EndZ=0
    g3: LineSegment StartX=-17 StartY=10.1 StartZ=0 EndX=-17 EndY=6.9 EndZ=0
    g4: ArcOfCircle CenterX=-15.5 CenterY=6.9 CenterZ=0 NormalX=0 NormalY=0 NormalZ=1 AngleXU=0 Radius=1.5 StartAngle=3.14159 EndAngle=6.28319
    g5: LineSegment StartX=-18.75 StartY=10.1 StartZ=0 EndX=-18.75 EndY=5.1 EndZ=0
    g6: LineSegment StartX=-18.75 StartY=5.1 StartZ=0 EndX=-12.25 EndY=5.1 EndZ=0
    g7: LineSegment StartX=-12.25 StartY=10.1 StartZ=0 EndX=-12.25 EndY=5.1 EndZ=0
  constraints (25):
    c: PointOnObject(g0,g-9)
    c: Horizontal(g0)
    c: PointOnObject(g1,g-3)
    c: Horizontal(g1)
    c: Coincident(g2,g1)
    c: Vertical(g2)
    c: Coincident(g3,g0)
    c: Vertical(g3)
    c: Coincident(g4,g3)
    c: Coincident(g4,g2)
    c: Coincident(g5,g0)
    c: PointOnObject(g5,g-10)
    c: Vertical(g5)
    c: PointOnObject(g6,g-6)
    c: Coincident(g7,g6)
    c: Vertical(g7)
    c: Coincident(g7,g1)
    c: Coincident(g6,g5)
    c: DistanceX(g0,g1) = 3
    c: DistanceX(g0,g0) = 1.75
    c: DistanceX(g1,g1) = 1.75
    c: DistanceY(g4,g3) = 0
    c: DistanceY(g4,g2) = 0
    c: DistanceX(g-7,g4) = 0
    c: DistanceY(g4,g-7) = 0.6
FEATURE [PartDesign::Pad] Pad009
  BaseFeature = -> Pocket009
  Direction = (0,-1,2e-16)
  Length = 0.8
  Length2 = 10
  Profile = -> Sketch019
  ReferenceAxis = -> Sketch019 [N_Axis]
  Refine = true
  Suppressed = false
  Type = 0
FEATURE [Sketcher::SketchObject] Sketch020
  ArcFitTolerance = 1e-06
  AttachmentSupport = -> [Pad009]
  ExternalGeometry = -> [Pad009]
  FullyConstrained = true
  MakeInternals = false
  MapMode = 5
  Placement = pos=(0,-2.5,0) rot=(0,0.707107,0.707107;3.14159rad)
  sketch-geometry (8):
    g0: LineSegment StartX=12.25 StartY=10.1 StartZ=0 EndX=14 EndY=10.1 EndZ=0
    g1: LineSegment StartX=18.75 StartY=10.1 StartZ=0 EndX=17 EndY=10.1 EndZ=0
    g2: LineSegment StartX=17 StartY=10.1 StartZ=0 EndX=17 EndY=6.9 EndZ=0
    g3: LineSegment StartX=14 StartY=10.1 StartZ=0 EndX=14 EndY=6.9 EndZ=0
    g4: ArcOfCircle CenterX=15.5 CenterY=6.9 CenterZ=0 NormalX=0 NormalY=0 NormalZ=1 AngleXU=0 Radius=1.5 StartAngle=3.14159 EndAngle=6.28319
    g5: LineSegment StartX=12.25 StartY=10.1 StartZ=0 EndX=12.25 EndY=5.1 EndZ=0
    g6: LineSegment StartX=18.75 StartY=10.1 StartZ=0 EndX=18.75 EndY=5.1 EndZ=0
    g7: LineSegment StartX=18.75 StartY=5.1 StartZ=0 EndX=12.25 EndY=5.1 EndZ=0
  constraints (25):
    c: PointOnObject(g0,g-3)
    c: Horizontal(g0)
    c: PointOnObject(g1,g-8)
    c: Horizontal(g1)
    c: Coincident(g2,g1)
    c: Vertical(g2)
    c: Coincident(g3,g0)
    c: Vertical(g3)
    c: Coincident(g4,g3)
    c: Coincident(g4,g2)
    c: Coincident(g5,g0)
    c: PointOnObject(g5,g-10)
    c: Vertical(g5)
    c: Coincident(g6,g1)
    c: PointOnObject(g6,g-9)
    c: Vertical(g6)
    c: Coincident(g7,g6)
    c: Coincident(g7,g5)
    c: DistanceX(g0,g1) = 3
    c: DistanceX(g0,g0) = 1.75
    c: DistanceX(g1,g1) = 1.75
    c: DistanceX(g-6,g4) = 0
    c: DistanceY(g4,g-6) = 0.6
    c: DistanceY(g4,g2) = 0
    c: DistanceY(g4,g3) = 0
FEATURE [PartDesign::Pad] Pad010
  BaseFeature = -> Pad009
  Direction = (0,1,-2e-16)
  Length = 0.8
  Length2 = 10
  Profile = -> Sketch020
  ReferenceAxis = -> Sketch020 [N_Axis]
  Refine = true
  Suppressed = false
  Type = 0
FEATURE [Sketcher::SketchObject] Sketch021
  ArcFitTolerance = 1e-06
  AttachmentSupport = -> [Pad010]
  ExternalGeometry = -> [Pad010]
  FullyConstrained = true
  MakeInternals = false
  MapMode = 5
  Placement = pos=(0,4,0) rot=(0,0.707107,0.707107;3.14159rad)
  sketch-geometry (8):
    g0: LineSegment StartX=26.1 StartY=10.1 StartZ=0 EndX=25 EndY=10.1 EndZ=0
    g1: LineSegment StartX=26.1 StartY=10.1 StartZ=0 EndX=26.1 EndY=7.49999 EndZ=0
    g2: LineSegment StartX=22.2 StartY=10.1 StartZ=0 EndX=21.1 EndY=10.1 EndZ=0
    g3: LineSegment StartX=22.2 StartY=10.1 StartZ=0 EndX=22.2 EndY=7.5 EndZ=0
    g4: LineSegment StartX=25 StartY=10.1 StartZ=0 EndX=25 EndY=7.5 EndZ=0
    g5: LineSegment StartX=21.1 StartY=10.1 StartZ=0 EndX=21.1 EndY=7.5 EndZ=0
    g6: ArcOfCircle CenterX=23.6 CenterY=7.5 CenterZ=0 NormalX=0 NormalY=0 NormalZ=1 AngleXU=0 Radius=1.4 StartAngle=3.14159 EndAngle=6.28319
    g7: ArcOfCircle CenterX=23.6 CenterY=7.5 CenterZ=0 NormalX=0 NormalY=0 NormalZ=1 AngleXU=0 Radius=2.5 StartAngle=3.14159 EndAngle=6.28318
  constraints (24):
    c: Coincident(g0,g-4)
    c: PointOnObject(g0,g-3)
    c: Coincident(g1,g0)
    c: PointOnObject(g1,g-4)
    c: PointOnObject(g2,g-3)
    c: PointOnObject(g2,g-3)
    c: Coincident(g3,g2)
    c: Vertical(g3)
    c: Coincident(g4,g0)
    c: Vertical(g4)
    c: Coincident(g5,g2)
    c: Vertical(g5)
    c: Coincident(g6,g4)
    c: Coincident(g6,g3)
    c: Coincident(g7,g1)
    c: Coincident(g7,g5)
    c: DistanceX(g0,g0) = 1.1
    c: DistanceX(g2,g2) = 1.1
    c: Coincident(g6,g7)
    c: DistanceX(g2,g0) = 5
    c: DistanceY(g3,g6) = 0
    c: DistanceY(g4,g6) = 0
    c: DistanceY(g6,g5) = 0
    c: DistanceY(g-4,g6) = 4.1
FEATURE [PartDesign::Pad] Pad011
  BaseFeature = -> Pad010
  Direction = (0,1,-2e-16)
  Length = 3.1
  Length2 = 10
  Profile = -> Sketch021
  ReferenceAxis = -> Sketch021 [N_Axis]
  Refine = true
  Suppressed = false
  Type = 0
FEATURE [PartDesign::Body] Body  label="Lower_Torso"
  AllowCompound = false
  Group = -> [Sketch,Pad,Sketch001,Pad001,Sketch002,Pocket,Sketch003,Pocket001,Sketch004,Pad002,Sketch005,Pocket002,Sketch006,Pocket003,Sketch007,Pocket004,Sketch008,Pad003,Sketch009,Pad004,Sketch010,Pocket005,Sketch011,Pocket006,Sketch012,Pocket007,Sketch013,Pad005,Sketch014,Pad006,Sketch015,Pad007,Sketch016,Pad008,Sketch017,Pocket008,Sketch018,Pocket009,Sketch019,Pad009,Sketch020,Pad010,Sketch021,Pad011,+77 more]
  Origin = -> Origin
  Tip = -> Pad243
COMPONENT P1 — recipe-attached ("Upper_Torso", modeled in this document).
Construction recipe (the document's own serialized feature program — sketch geometry with constraints, then the solid features built on it; lengths are millimeters unless a unit is written):

FEATURE [PartDesign::SubShapeBinder] Binder
  BindCopyOnChange = 0
  BindMode = 2
  ClaimChildren = false
  Context = -> Body001 [Binder.]
  Fuse = false
  MakeFace = true
  OffsetFill = false
  OffsetIntersection = false
  OffsetJoinType = 0
  OffsetOpenResult = false
  PartialLoad = false
  Refine = true
  Relative = true
  _Version = 2
FEATURE [Sketcher::SketchObject] Sketch039
  ArcFitTolerance = 1e-06
  AttachmentSupport = -> [Binder]
  FullyConstrained = true
  MakeInternals = false
  MapMode = 5
  Placement = pos=(0,0,10.1) rot=(0,0,1;0rad)
  sketch-geometry (12):
    g0: LineSegment StartX=10.3 StartY=18.5 StartZ=0 EndX=-18.7 EndY=18.5 EndZ=0
    g1: LineSegment StartX=-18.7 StartY=18.5 StartZ=0 EndX=-18.7 EndY=16 EndZ=0
    g2: LineSegment StartX=-18.7 StartY=16 StartZ=0 EndX=-30.4 EndY=16 EndZ=0
    g3: LineSegment StartX=-30.4 StartY=16 StartZ=0 EndX=-30.4 EndY=11 EndZ=0
    g4: LineSegment StartX=-30.4 StartY=11 StartZ=0 EndX=-27.5 EndY=11 EndZ=0
    g5: LineSegment StartX=-27.5 StartY=11 StartZ=0 EndX=-27.5 EndY=-11 EndZ=0
    g6: LineSegment StartX=-27.5 StartY=-11 StartZ=0 EndX=-30.4 EndY=-11 EndZ=0
    g7: LineSegment StartX=-30.4 StartY=-11 StartZ=0 EndX=-30.4 EndY=-16 EndZ=0
    g8: LineSegment StartX=-30.4 StartY=-16 StartZ=0 EndX=-18.7 EndY=-16 EndZ=0
    g9: LineSegment StartX=-18.7 StartY=-16 StartZ=0 EndX=-18.7 EndY=-18.5 EndZ=0
    g10: LineSegment StartX=-18.7 StartY=-18.5 StartZ=0 EndX=10.3 EndY=-18.5 EndZ=0
    g11: LineSegment StartX=10.3 StartY=-18.5 StartZ=0 EndX=10.3 EndY=18.5 EndZ=0
  constraints (38):
    c: Horizontal(g0)
    c: Coincident(g1,g0)
    c: Vertical(g1)
    c: Coincident(g2,g1)
    c: Horizontal(g2)
    c: Coincident(g3,g2)
    c: Vertical(g3)
    c: Coincident(g4,g3)
    c: Horizontal(g4)
    c: Coincident(g5,g4)
    c: Vertical(g5)
    c: Coincident(g6,g5)
    c: Horizontal(g6)
    c: Coincident(g7,g6)
    c: Vertical(g7)
    c: Coincident(g8,g7)
    c: Horizontal(g8)
    c: Coincident(g9,g8)
    c: Vertical(g9)
    c: Coincident(g10,g9)
    c: Horizontal(g10)
    c: Coincident(g11,g10)
    c: Coincident(g11,g0)
    c: Vertical(g11)
    c: DistanceY(g11,g11) = 37
    c: DistanceX(g0,g0) = 29
    c: DistanceX(g10,g10) = 29
    c: DistanceY(g7,g7) = 5
    c: DistanceY(g3,g3) = 5
    c: DistanceY(g5,g5) = 22
    c: DistanceY(g1,g1) = 2.5
    c: DistanceY(g9,g9) = 2.5
    c: DistanceX(g8,g8) = 11.7
    c: DistanceX(g2,g2) = 11.7
    c: DistanceX(g4,g4) = 2.9
    c: DistanceX(g7,g10) = 40.7
    c: DistanceY(g-1,g0) = 18.5
    c: DistanceX(g4,g-1) = 27.5
FEATURE [PartDesign::Pad] Pad021
  Direction = (0,0,1)
  Length = 1.5
  Length2 = 10
  Profile = -> Sketch039
  ReferenceAxis = -> Sketch039 [N_Axis]
  Refine = true
  Suppressed = false
  Type = 0
FEATURE [Sketcher::SketchObject] Sketch040
  ArcFitTolerance = 1e-06
  AttachmentSupport = -> [Pad021]
  ExternalGeometry = -> [Pad021]
  FullyConstrained = true
  MakeInternals = false
  MapMode = 5
  Placement = pos=(0,0,11.6) rot=(0,0,1;0rad)
  sketch-geometry (4):
    g0: LineSegment StartX=-24.75 StartY=2.5 StartZ=0 EndX=-24.75 EndY=-2.5 EndZ=0
    g1: LineSegment StartX=-24.75 StartY=-2.5 StartZ=0 EndX=-20.35 EndY=-2.5 EndZ=0
    g2: LineSegment StartX=-20.35 StartY=-2.5 StartZ=0 EndX=-20.35 EndY=2.5 EndZ=0
    g3: LineSegment StartX=-20.35 StartY=2.5 StartZ=0 EndX=-24.75 EndY=2.5 EndZ=0
  constraints (12):
    c: Coincident(g0,g1)
    c: Coincident(g1,g2)
    c: Coincident(g2,g3)
    c: Coincident(g3,g0)
    c: Vertical(g0)
    c: Vertical(g2)
    c: Horizontal(g1)
    c: Horizontal(g3)
    c: DistanceX(g3,g3) = 4.4
    c: DistanceY(g2,g2) = 5
    c: DistanceY(g-1,g2) = 2.5
    c: DistanceX(g-3,g0) = 2.75
FEATURE [PartDesign::Pocket] Pocket021
  BaseFeature = -> Pad021
  Direction = (0,0,-1)
  Length = 5
  Length2 = 5
  Profile = -> Sketch040
  ReferenceAxis = -> Sketch040 [N_Axis]
  Refine = true
  Suppressed = false
  Type = 0
FEATURE [Sketcher::SketchObject] Sketch043
  ArcFitTolerance = 1e-06
  AttachmentSupport = -> [Pocket021]
  ExternalGeometry = -> [Pocket021]
  FullyConstrained = true
  MakeInternals = false
  MapMode = 5
  Placement = pos=(0,0,11.6) rot=(0,0,1;0rad)
  sketch-geometry (4):
    g0: LineSegment StartX=10.3 StartY=5.3 StartZ=0 EndX=-12.65 EndY=5.3 EndZ=0
    g1: LineSegment StartX=-12.65 StartY=5.3 StartZ=0 EndX=-12.65 EndY=-5.3 EndZ=0
    g2: LineSegment StartX=-12.65 StartY=-5.3 StartZ=0 EndX=10.3 EndY=-5.3 EndZ=0
    g3: LineSegment StartX=10.3 StartY=-5.3 StartZ=0 EndX=10.3 EndY=5.3 EndZ=0
  constraints (12):
    c: Coincident(g0,g1)
    c: Coincident(g1,g2)
    c: Coincident(g2,g3)
    c: Coincident(g3,g0)
    c: Horizontal(g0)
    c: Horizontal(g2)
    c: Vertical(g1)
    c: Vertical(g3)
    c: PointOnObject(g0,g-3)
    c: DistanceY(g1,g1) = 10.6
    c: DistanceY(g-1,g0) = 5.3
    c: DistanceX(g-4,g0) = 7.7
FEATURE [PartDesign::Pocket] Pocket022
  BaseFeature = -> Pocket021
  Direction = (0,0,-1)
  Length = 5
  Length2 = 5
  Profile = -> Sketch043
  ReferenceAxis = -> Sketch043 [N_Axis]
  Refine = true
  Suppressed = false
  Type = 0
FEATURE [Sketcher::SketchObject] Sketch044
  ArcFitTolerance = 1e-06
  AttachmentSupport = -> [Pocket022]
  ExternalGeometry = -> [Pocket022]
  FullyConstrained = true
  MakeInternals = false
  MapMode = 5
  Placement = pos=(0,0,11.6) rot=(0,0,1;0rad)
  sketch-geometry (8):
    g0: LineSegment StartX=-28.4 StartY=-16 StartZ=0 EndX=-25.3 EndY=-16 EndZ=0
    g1: LineSegment StartX=-25.3 StartY=-16 StartZ=0 EndX=-25.3 EndY=-12.5 EndZ=0
    g2: LineSegment StartX=-25.3 StartY=-12.5 StartZ=0 EndX=-28.4 EndY=-12.5 EndZ=0
    g3: LineSegment StartX=-28.4 StartY=-12.5 StartZ=0 EndX=-28.4 EndY=-16 EndZ=0
    g4: LineSegment StartX=-28.4 StartY=16 StartZ=0 EndX=-28.4 EndY=12.5 EndZ=0
    g5: LineSegment StartX=-28.4 StartY=12.5 StartZ=0 EndX=-25.3 EndY=12.5 EndZ=0
    g6: LineSegment StartX=-25.3 StartY=12.5 StartZ=0 EndX=-25.3 EndY=16 EndZ=0
    g7: LineSegment StartX=-25.3 StartY=16 StartZ=0 EndX=-28.4 EndY=16 EndZ=0
  constraints (24):
    c: Coincident(g0,g1)
    c: Coincident(g1,g2)
    c: Coincident(g2,g3)
    c: Coincident(g3,g0)
    c: Horizontal(g0)
    c: Horizontal(g2)
    c: Vertical(g1)
    c: Vertical(g3)
    c: PointOnObject(g0,g-4)
    c: Coincident(g4,g5)
    c: Coincident(g5,g6)
    c: Coincident(g6,g7)
    c: Coincident(g7,g4)
    c: Vertical(g4)
    c: Vertical(g6)
    c: Horizontal(g5)
    c: Horizontal(g7)
    c: PointOnObject(g4,g-3)
    c: DistanceX(g-3,g4) = 2
    c: DistanceX(g-4,g0) = 2
    c: DistanceX(g2,g2) = 3.1
    c: DistanceX(g5,g5) = 3.1
    c: DistanceY(g6,g6) = 3.5
    c: DistanceY(g1,g1) = 3.5
FEATURE [PartDesign::Pocket] Pocket023
  BaseFeature = -> Pocket022
  Direction = (0,0,-1)
  Length = 5
  Length2 = 5
  Profile = -> Sketch044
  ReferenceAxis = -> Sketch044 [N_Axis]
  Refine = true
  Suppressed = false
  Type = 0
FEATURE [Sketcher::SketchObject] Sketch045
  ArcFitTolerance = 1e-06
  AttachmentSupport = -> [Pocket023]
  ExternalGeometry = -> [Pocket023]
  FullyConstrained = true
  MakeInternals = false
  MapMode = 5
  Placement = pos=(0,0,11.6) rot=(0,0,1;0rad)
  sketch-geometry (4):
    g0: LineSegment StartX=-18.7 StartY=-8.8 StartZ=0 EndX=-18.7 EndY=-14.8 EndZ=0
    g1: LineSegment StartX=-18.7 StartY=-14.8 StartZ=0 EndX=-12.7 EndY=-14.8 EndZ=0
    g2: LineSegment StartX=-12.7 StartY=-14.8 StartZ=0 EndX=-12.7 EndY=-8.8 EndZ=0
    g3: LineSegment StartX=-12.7 StartY=-8.8 StartZ=0 EndX=-18.7 EndY=-8.8 EndZ=0
  constraints (12):
    c: Coincident(g0,g1)
    c: Coincident(g1,g2)
    c: Coincident(g2,g3)
    c: Coincident(g3,g0)
    c: Vertical(g0)
    c: Vertical(g2)
    c: Horizontal(g1)
    c: Horizontal(g3)
    c: DistanceX(g3,g3) = 6
    c: DistanceY(g2,g2) = 6
    c: DistanceY(g-3,g0) = 3.7
    c: DistanceX(g-3,g0) = 0
FEATURE [PartDesign::Pad] Pad022
  BaseFeature = -> Pocket023
  Direction = (0,0,1)
  Length = 1
  Length2 = 10
  Profile = -> Sketch045
  ReferenceAxis = -> Sketch045 [N_Axis]
  Refine = true
  Suppressed = false
  Type = 0
FEATURE [Sketcher::SketchObject] Sketch046
  ArcFitTolerance = 1e-06
  AttachmentSupport = -> [Pad022]
  ExternalGeometry = -> [Pad022]
  FullyConstrained = true
  MakeInternals = false
  MapMode = 5
  Placement = pos=(0,0,12.6) rot=(0,0,1;0rad)
  sketch-geometry (1):
    g0: Circle CenterX=-15.7 CenterY=-11.8 CenterZ=0 NormalX=0 NormalY=0 NormalZ=1 AngleXU=0 Radius=1.35
  constraints (3):
    c: Diameter(g0) = 2.7
    c: DistanceX(g-5,g0) = 3
    c: DistanceY(g0,g-4) = 3
FEATURE [PartDesign::Pocket] Pocket024
  BaseFeature = -> Pad022
  Direction = (0,0,-1)
  Length = 5
  Length2 = 5
  Profile = -> Sketch046
  ReferenceAxis = -> Sketch046 [N_Axis]
  Refine = true
  Suppressed = false
  Type = 0
FEATURE [Sketcher::SketchObject] Sketch047
  ArcFitTolerance = 1e-06
  AttachmentSupport = -> [Pocket024]
  ExternalGeometry = -> [Pocket024]
  FullyConstrained = true
  MakeInternals = false
  MapMode = 5
  Placement = pos=(0,0,11.6) rot=(0,0,1;0rad)
  sketch-geometry (4):
    g0: LineSegment StartX=-14.4 StartY=-4.55 StartZ=0 EndX=-16.6 EndY=-4.55 EndZ=0
    g1: LineSegment StartX=-16.6 StartY=-4.55 StartZ=0 EndX=-16.6 EndY=-7.8 EndZ=0
    g2: LineSegment StartX=-16.6 StartY=-7.8 StartZ=0 EndX=-14.4 EndY=-7.8 EndZ=0
    g3: LineSegment StartX=-14.4 StartY=-7.8 StartZ=0 EndX=-14.4 EndY=-4.55 EndZ=0
  constraints (12):
    c: Coincident(g0,g1)
    c: Coincident(g1,g2)
    c: Coincident(g2,g3)
    c: Coincident(g3,g0)
    c: Horizontal(g0)
    c: Horizontal(g2)
    c: Vertical(g1)
    c: Vertical(g3)
    c: DistanceX(g-3,g1) = 10.9
    c: DistanceX(g0,g0) = 2.2
    c: DistanceY(g3,g3) = 3.25
    c: DistanceY(g-4,g2) = 10.7
FEATURE [PartDesign::Pocket] Pocket025
  BaseFeature = -> Pocket024
  Direction = (0,0,-1)
  Length = 5
  Length2 = 5
  Profile = -> Sketch047
  ReferenceAxis = -> Sketch047 [N_Axis]
  Refine = true
  Suppressed = false
  Type = 0
FEATURE [Sketcher::SketchObject] Sketch048
  ArcFitTolerance = 1e-06
  AttachmentSupport = -> [Pocket025]
  ExternalGeometry = -> [Pocket025]
  FullyConstrained = true
  MakeInternals = false
  MapMode = 5
  Placement = pos=(0,0,11.6) rot=(0,0,1;0rad)
  sketch-geometry (9):
    g0: Circle CenterX=-5.8 CenterY=-11.8 CenterZ=0 NormalX=0 NormalY=0 NormalZ=1 AngleXU=0 Radius=0.65
    g1: LineSegment StartX=-20.4 StartY=14.5 StartZ=0 EndX=-20.4 EndY=9.1 EndZ=0
    g2: LineSegment StartX=-20.4 StartY=9.1 StartZ=0 EndX=-15.3 EndY=9.1 EndZ=0
    g3: LineSegment StartX=-15.3 StartY=9.1 StartZ=0 EndX=-15.3 EndY=14.5 EndZ=0
    g4: LineSegment StartX=-15.3 StartY=14.5 StartZ=0 EndX=-20.4 EndY=14.5 EndZ=0
    g5: LineSegment StartX=-2.5 StartY=14.5 StartZ=0 EndX=-2.5 EndY=9.7 EndZ=0
    g6: LineSegment StartX=-2.5 StartY=9.7 StartZ=0 EndX=2.6 EndY=9.7 EndZ=0
    g7: LineSegment StartX=2.6 StartY=9.7 StartZ=0 EndX=2.6 EndY=14.5 EndZ=0
    g8: LineSegment StartX=2.6 StartY=14.5 StartZ=0 EndX=-2.5 EndY=14.5 EndZ=0
  constraints (28):
    c: Coincident(g1,g2)
    c: Coincident(g2,g3)
    c: Coincident(g3,g4)
    c: Coincident(g4,g1)
    c: Vertical(g1)
    c: Vertical(g3)
    c: Horizontal(g2)
    c: Horizontal(g4)
    c: Coincident(g5,g6)
    c: Coincident(g6,g7)
    c: Coincident(g7,g8)
    c: Coincident(g8,g5)
    c: Vertical(g5)
    c: Vertical(g7)
    c: Horizontal(g6)
    c: Horizontal(g8)
    c: Diameter(g0) = 1.3
    c: DistanceY(g-3,g0) = 0
    c: DistanceY(g3,g3) = 5.4
    c: DistanceY(g5,g5) = 4.8
    c: DistanceX(g4,g4) = 5.1
    c: DistanceX(g8,g8) = 5.1
    c: DistanceY(g1,g-4) = 4
    c: DistanceY(g7,g-4) = 4
    c: DistanceX(g3,g5) = 12.8
    c: Radius(g-3) = 1.35
    c: DistanceX(g-3,g0) = 9.9
    c: DistanceX(g-5,g1) = 7.1
FEATURE [PartDesign::Pocket] Pocket026
  BaseFeature = -> Pocket025
  Direction = (0,0,-1)
  Length = 5
  Length2 = 5
  Profile = -> Sketch048
  ReferenceAxis = -> Sketch048 [N_Axis]
  Refine = true
  Suppressed = false
  Type = 0
FEATURE [Sketcher::SketchObject] Sketch049
  ArcFitTolerance = 1e-06
  AttachmentSupport = -> [Pocket026]
  ExternalGeometry = -> [Pocket026]
  FullyConstrained = true
  MakeInternals = false
  MapMode = 5
  Placement = pos=(0,0,11.6) rot=(0,0,1;0rad)
  sketch-geometry (8):
    g0: LineSegment StartX=-21.8 StartY=16 StartZ=0 EndX=-21.8 EndY=8.5 EndZ=0
    g1: LineSegment StartX=-21.8 StartY=8.5 StartZ=0 EndX=-18.7 EndY=8.5 EndZ=0
    g2: LineSegment StartX=-18.7 StartY=8.5 StartZ=0 EndX=-18.7 EndY=16 EndZ=0
    g3: LineSegment StartX=-18.7 StartY=16 StartZ=0 EndX=-21.8 EndY=16 EndZ=0
    g4: LineSegment StartX=3 StartY=15.2 StartZ=0 EndX=0.2 EndY=15.2 EndZ=0
    g5: LineSegment StartX=0.2 StartY=15.2 StartZ=0 EndX=0.2 EndY=7 EndZ=0
    g6: LineSegment StartX=0.2 StartY=7 StartZ=0 EndX=3 EndY=7 EndZ=0
    g7: LineSegment StartX=3 StartY=7 StartZ=0 EndX=3 EndY=15.2 EndZ=0
  constraints (24):
    c: Coincident(g0,g1)
    c: Coincident(g1,g2)
    c: Coincident(g2,g3)
    c: Coincident(g3,g0)
    c: Vertical(g0)
    c: Vertical(g2)
    c: Horizontal(g1)
    c: Horizontal(g3)
    c: Coincident(g4,g5)
    c: Coincident(g5,g6)
    c: Coincident(g6,g7)
    c: Coincident(g7,g4)
    c: Horizontal(g4)
    c: Horizontal(g6)
    c: Vertical(g5)
    c: Vertical(g7)
    c: DistanceY(g0,g0) = 7.5
    c: DistanceX(g3,g3) = 3.1
    c: Coincident(g2,g-9)
    c: DistanceY(g7,g7) = 8.2
    c: DistanceY(g4,g-10) = 3.3
    c: DistanceX(g4,g4) = 2.8
    c: DistanceX(g-11,g5) = 27.7
    c: DistanceY(g-12,g6) = 1.7
FEATURE [PartDesign::Pad] Pad023
  BaseFeature = -> Pocket026
  Direction = (0,0,1)
  Length = 1.5
  Length2 = 10
  Profile = -> Sketch049
  ReferenceAxis = -> Sketch049 [N_Axis]
  Refine = true
  Suppressed = false
  Type = 0
FEATURE [Sketcher::SketchObject] Sketch050
  ArcFitTolerance = 1e-06
  AttachmentSupport = -> [Pad023]
  ExternalGeometry = -> [Pad023]
  FullyConstrained = true
  MakeInternals = false
  MapMode = 5
  Placement = pos=(0,-16,0) rot=(1,0,0;1.5708rad)
  sketch-geometry (8):
    g0: LineSegment StartX=-30.4 StartY=11.6 StartZ=0 EndX=-28.4 EndY=11.6 EndZ=0
    g1: LineSegment StartX=-25.3 StartY=11.6 StartZ=0 EndX=-23.3 EndY=11.6 EndZ=0
    g2: LineSegment StartX=-25.3 StartY=11.6 StartZ=0 EndX=-25.3 EndY=14.55 EndZ=0
    g3: LineSegment StartX=-28.4 StartY=11.6 StartZ=0 EndX=-28.4 EndY=14.55 EndZ=0
    g4: LineSegment StartX=-30.4 StartY=11.6 StartZ=0 EndX=-30.4 EndY=14.55 EndZ=0
    g5: LineSegment StartX=-23.3 StartY=11.6 StartZ=0 EndX=-23.3 EndY=14.55 EndZ=0
    g6: ArcOfCircle CenterX=-26.85 CenterY=14.55 CenterZ=0 NormalX=0 NormalY=0 NormalZ=1 AngleXU=0 Radius=1.55 StartAngle=5e-16 EndAngle=3.1416
    g7: ArcOfCircle CenterX=-26.85 CenterY=14.55 CenterZ=0 NormalX=0 NormalY=0 NormalZ=1 AngleXU=0 Radius=3.55 StartAngle=1e-16 EndAngle=3.1416
  constraints (22):
    c: Coincident(g0,g-3)
    c: Coincident(g0,g-3)
    c: Coincident(g1,g-4)
    c: PointOnObject(g1,g-4)
    c: Coincident(g2,g1)
    c: Vertical(g2)
    c: Coincident(g3,g0)
    c: Vertical(g3)
    c: Coincident(g4,g0)
    c: Vertical(g4)
    c: Coincident(g5,g1)
    c: Vertical(g5)
    c: Coincident(g6,g3)
    c: Coincident(g6,g2)
    c: Coincident(g7,g4)
    c: Coincident(g7,g5)
    c: DistanceX(g1,g1) = 2
    c: Diameter(g6) = 3.1
    c: Coincident(g6,g7)
    c: DistanceY(g6,g2) = 0
    c: DistanceY(g2,g5) = 0
    c: DistanceY(g0,g6) = 2.95
FEATURE [PartDesign::Pad] Pad024
  BaseFeature = -> Pad023
  Direction = (0,-1,2e-16)
  Length = 2.75
  Length2 = 10
  Profile = -> Sketch050
  ReferenceAxis = -> Sketch050 [N_Axis]
  Refine = true
  Reversed = true
  Suppressed = false
  Type = 0
FEATURE [Sketcher::SketchObject] Sketch051
  ArcFitTolerance = 1e-06
  AttachmentSupport = -> [Pad024]
  ExternalGeometry = -> [Pad024]
  FullyConstrained = false
  MakeInternals = false
  MapMode = 5
  Placement = pos=(0,16,0) rot=(0,0.707107,0.707107;3.14159rad)
  sketch-geometry (8):
    g0: LineSegment StartX=28.4 StartY=11.6 StartZ=0 EndX=30.4 EndY=11.6 EndZ=0
    g1: LineSegment StartX=25.3 StartY=11.6 StartZ=0 EndX=23.3 EndY=11.6 EndZ=0
    g2: LineSegment StartX=23.3 StartY=11.6 StartZ=0 EndX=23.3 EndY=14.55 EndZ=0
    g3: LineSegment StartX=25.3 StartY=11.6 StartZ=0 EndX=25.3 EndY=14.55 EndZ=0
    g4: LineSegment StartX=28.4 StartY=11.6 StartZ=0 EndX=28.4 EndY=14.55 EndZ=0
    g5: LineSegment StartX=30.4 StartY=11.6 StartZ=0 EndX=30.4 EndY=14.55 EndZ=0
    g6: ArcOfCircle CenterX=26.85 CenterY=14.55 CenterZ=0 NormalX=0 NormalY=0 NormalZ=1 AngleXU=0 Radius=1.55 StartAngle=6.28318 EndAngle=9.42478
    g7: ArcOfCircle CenterX=26.85 CenterY=14.55 CenterZ=0 NormalX=0 NormalY=0 NormalZ=1 AngleXU=0 Radius=3.55 StartAngle=6.28318 EndAngle=9.42478
  constraints (16):
    c: Coincident(g0,g-3)
    c: Coincident(g0,g-3)
    c: Coincident(g1,g-6)
    c: Coincident(g1,g-5)
    c: Coincident(g2,g1)
    c: Coincident(g2,g-10)
    c: Coincident(g3,g1)
    c: Coincident(g3,g-7)
    c: Coincident(g4,g0)
    c: Coincident(g4,g-8)
    c: Coincident(g5,g0)
    c: Coincident(g5,g-10)
    c: Coincident(g6,g3)
    c: Coincident(g6,g4)
    c: Coincident(g7,g2)
    c: Tangent(g7,g-10) = -1.5708
FEATURE [PartDesign::Pad] Pad025
  BaseFeature = -> Pad024
  Direction = (0,1,-2e-16)
  Length = 2.75
  Length2 = 10
  Profile = -> Sketch051
  ReferenceAxis = -> Sketch051 [N_Axis]
  Refine = true
  Reversed = true
  Suppressed = false
  Type = 0
FEATURE [Sketcher::SketchObject] Sketch052
  ArcFitTolerance = 1e-06
  AttachmentSupport = -> [Pad025]
  ExternalGeometry = -> [Pad025]
  FullyConstrained = true
  MakeInternals = false
  MapMode = 5
  Placement = pos=(0,0,10.1) rot=(1,0,0;3.14159rad)
  sketch-geometry (8):
    g0: LineSegment StartX=-7.05 StartY=-5.3 StartZ=0 EndX=-7.05 EndY=-6.8 EndZ=0
    g1: LineSegment StartX=-7.05 StartY=-6.8 StartZ=0 EndX=0.95 EndY=-6.8 EndZ=0
    g2: LineSegment StartX=0.95 StartY=-6.8 StartZ=0 EndX=0.95 EndY=-5.3 EndZ=0
    g3: LineSegment StartX=0.95 StartY=-5.3 StartZ=0 EndX=-7.05 EndY=-5.3 EndZ=0
    g4: LineSegment StartX=-7.05 StartY=5.3 StartZ=0 EndX=0.95 EndY=5.3 EndZ=0
    g5: LineSegment StartX=0.95 StartY=5.3 StartZ=0 EndX=0.95 EndY=6.8 EndZ=0
    g6: LineSegment StartX=0.95 StartY=6.8 StartZ=0 EndX=-7.05 EndY=6.8 EndZ=0
    g7: LineSegment StartX=-7.05 StartY=6.8 StartZ=0 EndX=-7.05 EndY=5.3 EndZ=0
  constraints (24):
    c: Coincident(g0,g1)
    c: Coincident(g1,g2)
    c: Coincident(g2,g3)
    c: Coincident(g3,g0)
    c: Vertical(g0)
    c: Vertical(g2)
    c: Horizontal(g1)
    c: Horizontal(g3)
    c: PointOnObject(g0,g-3)
    c: Coincident(g4,g5)
    c: Coincident(g5,g6)
    c: Coincident(g6,g7)
    c: Coincident(g7,g4)
    c: Horizontal(g4)
    c: Horizontal(g6)
    c: Vertical(g5)
    c: Vertical(g7)
    c: PointOnObject(g4,g-4)
    c: DistanceX(g6,g6) = 8
    c: DistanceX(g1,g1) = 8
    c: DistanceX(g-3,g0) = 5.6
    c: DistanceX(g-4,g4) = 5.6
    c: DistanceY(g5,g5) = 1.5
    c: DistanceY(g2,g2) = 1.5
FEATURE [PartDesign::Pad] Pad026
  BaseFeature = -> Pad025
  Direction = (0,0,-1)
  Length = 6.3
  Length2 = 10
  Profile = -> Sketch052
  ReferenceAxis = -> Sketch052 [N_Axis]
  Refine = true
  Suppressed = false
  Type = 0
FEATURE [Sketcher::SketchObject] Sketch053
  ArcFitTolerance = 1e-06
  AttachmentSupport = -> [Pad026]
  ExternalGeometry = -> [Pad026]
  FullyConstrained = true
  MakeInternals = false
  MapMode = 5
  Placement = pos=(0,0,3.8) rot=(1,0,0;3.14159rad)
  sketch-geometry (4):
    g0: LineSegment StartX=-7.05 StartY=6.8 StartZ=0 EndX=-7.05 EndY=-6.8 EndZ=0
    g1: LineSegment StartX=-7.05 StartY=-6.8 StartZ=0 EndX=0.95 EndY=-6.8 EndZ=0
    g2: LineSegment StartX=0.95 StartY=-6.8 StartZ=0 EndX=0.95 EndY=6.8 EndZ=0
    g3: LineSegment StartX=0.95 StartY=6.8 StartZ=0 EndX=-7.05 EndY=6.8 EndZ=0
  constraints (10):
    c: Coincident(g0,g1)
    c: Coincident(g1,g2)
    c: Coincident(g2,g3)
    c: Coincident(g3,g0)
    c: Vertical(g0)
    c: Vertical(g2)
    c: Horizontal(g1)
    c: Horizontal(g3)
    c: Coincident(g0,g-4)
    c: Coincident(g1,g-6)
FEATURE [PartDesign::Pad] Pad027
  BaseFeature = -> Pad026
  Direction = (0,0,-1)
  Length = 3
  Length2 = 10
  Profile = -> Sketch053
  ReferenceAxis = -> Sketch053 [N_Axis]
  Refine = true
  Reversed = true
  Suppressed = false
  Type = 0
FEATURE [Sketcher::SketchObject] Sketch054
  ArcFitTolerance = 1e-06
  AttachmentSupport = -> [Pad027]
  ExternalGeometry = -> [Pad027]
  FullyConstrained = true
  MakeInternals = false
  MapMode = 5
  Placement = pos=(0,0,6.8) rot=(0,0,1;0rad)
  sketch-geometry (1):
    g0: Circle CenterX=-2.5 CenterY=9e-16 CenterZ=0 NormalX=0 NormalY=0 NormalZ=1 AngleXU=0 Radius=0.75
  constraints (5):
    c: Radius(g0) = 0.75
    c: DistanceX(g-4,g-3) = 8
    c: DistanceY(g-3,g-3) = 10.6
    c: DistanceX(g-4,g0) = 4.55
    c: DistanceY(g0,g-3) = 5.3
FEATURE [PartDesign::Pocket] Pocket027
  BaseFeature = -> Pad027
  Direction = (0,0,-1)
  Length = 5
  Length2 = 5
  Profile = -> Sketch054
  ReferenceAxis = -> Sketch054 [N_Axis]
  Refine = true
  Suppressed = false
  Type = 0
FEATURE [Sketcher::SketchObject] Sketch055
  ArcFitTolerance = 1e-06
  AttachmentSupport = -> [Pocket027]
  ExternalGeometry = -> [Pocket027]
  FullyConstrained = true
  MakeInternals = false
  MapMode = 5
  Placement = pos=(0,0,11.6) rot=(0,0,1;0rad)
  sketch-geometry (4):
    g0: LineSegment StartX=0.2 StartY=5.3 StartZ=0 EndX=-1.75 EndY=5.3 EndZ=0
    g1: LineSegment StartX=-1.75 StartY=5.3 StartZ=0 EndX=-1.75 EndY=-5.3 EndZ=0
    g2: LineSegment StartX=-1.75 StartY=-5.3 StartZ=0 EndX=0.2 EndY=-5.3 EndZ=0
    g3: LineSegment StartX=0.2 StartY=-5.3 StartZ=0 EndX=0.2 EndY=5.3 EndZ=0
  constraints (12):
    c: Coincident(g0,g1)
    c: Coincident(g2,g3)
    c: Coincident(g3,g0)
    c: Horizontal(g0)
    c: Horizontal(g2)
    c: Vertical(g1)
    c: Vertical(g3)
    c: DistanceX(g0,g0) = 1.95
    c: Coincident(g2,g1)
    c: DistanceX(g-3,g0) = 0
    c: PointOnObject(g0,g-4)
    c: PointOnObject(g2,g-5)
FEATURE [PartDesign::Pad] Pad028
  BaseFeature = -> Pocket027
  Direction = (0,0,1)
  Length = 4.8
  Length2 = 10
  Profile = -> Sketch055
  ReferenceAxis = -> Sketch055 [N_Axis]
  Refine = true
  Reversed = true
  Suppressed = false
  Type = 0
FEATURE [Sketcher::SketchObject] Sketch056
  ArcFitTolerance = 1e-06
  AttachmentSupport = -> [Pad028]
  ExternalGeometry = -> [Pad028]
  FullyConstrained = true
  MakeInternals = false
  MapMode = 5
  Placement = pos=(0,0,6.8) rot=(0,0,1;0rad)
  sketch-geometry (4):
    g0: LineSegment StartX=0.95 StartY=5.3 StartZ=0 EndX=0.2 EndY=5.3 EndZ=0
    g1: LineSegment StartX=0.2 StartY=5.3 StartZ=0 EndX=0.2 EndY=-5.3 EndZ=0
    g2: LineSegment StartX=0.2 StartY=-5.3 StartZ=0 EndX=0.95 EndY=-5.3 EndZ=0
    g3: LineSegment StartX=0.95 StartY=-5.3 StartZ=0 EndX=0.95 EndY=5.3 EndZ=0
  constraints (10):
    c: Coincident(g0,g1)
    c: Coincident(g1,g2)
    c: Coincident(g2,g3)
    c: Coincident(g3,g0)
    c: Horizontal(g0)
    c: Horizontal(g2)
    c: Vertical(g1)
    c: Coincident(g2,g-3)
    c: DistanceX(g2,g2) = 0.75
    c: Coincident(g-3,g0)
FEATURE [PartDesign::Pad] Pad029
  BaseFeature = -> Pad028
  Direction = (0,0,1)
  Length = 4.8
  Length2 = 10
  Profile = -> Sketch056
  ReferenceAxis = -> Sketch056 [N_Axis]
  Refine = true
  Suppressed = false
  Type = 0
FEATURE [Sketcher::SketchObject] Sketch057
  ArcFitTolerance = 1e-06
  AttachmentSupport = -> [Pad029]
  ExternalGeometry = -> [Pad029]
  FullyConstrained = true
  MakeInternals = false
  MapMode = 5
  Placement = pos=(0,0,11.6) rot=(0,0,1;0rad)
  sketch-geometry (4):
    g0: LineSegment StartX=-1.75 StartY=-5.3 StartZ=0 EndX=-17.75 EndY=-5.3 EndZ=0
    g1: LineSegment StartX=-17.75 StartY=-5.3 StartZ=0 EndX=-17.75 EndY=-6.8 EndZ=0
    g2: LineSegment StartX=-17.75 StartY=-6.8 StartZ=0 EndX=-1.75 EndY=-6.8 EndZ=0
    g3: LineSegment StartX=-1.75 StartY=-6.8 StartZ=0 EndX=-1.75 EndY=-5.3 EndZ=0
  constraints (11):
    c: Coincident(g0,g1)
    c: Coincident(g1,g2)
    c: Coincident(g2,g3)
    c: Coincident(g3,g0)
    c: Horizontal(g0)
    c: Horizontal(g2)
    c: Vertical(g1)
    c: Vertical(g3)
    c: Coincident(g0,g-3)
    c: DistanceY(g3,g3) = 1.5
    c: DistanceX(g2,g2) = 16
FEATURE [PartDesign::Pad] Pad030
  BaseFeature = -> Pad029
  Direction = (0,0,1)
  Length = 5
  Length2 = 10
  Profile = -> Sketch057
  ReferenceAxis = -> Sketch057 [N_Axis]
  Refine = true
  Suppressed = false
  Type = 0
FEATURE [Sketcher::SketchObject] Sketch058
  ArcFitTolerance = 1e-06
  AttachmentSupport = -> [Pad030]
  ExternalGeometry = -> [Pad030]
  FullyConstrained = true
  MakeInternals = false
  MapMode = 5
  Placement = pos=(0,-5.3,0) rot=(0,0.707107,0.707107;3.14159rad)
  sketch-geometry (4):
    g0: LineSegment StartX=16.6 StartY=11.6 StartZ=0 EndX=16.6 EndY=12.75 EndZ=0
    g1: LineSegment StartX=14.4 StartY=11.6 StartZ=0 EndX=14.4 EndY=12.75 EndZ=0
    g2: ArcOfCircle CenterX=15.5 CenterY=12.75 CenterZ=0 NormalX=0 NormalY=0 NormalZ=1 AngleXU=0 Radius=1.1 StartAngle=0 EndAngle=3.14159
    g3: LineSegment StartX=16.6 StartY=11.6 StartZ=0 EndX=14.4 EndY=11.6 EndZ=0
  constraints (12):
    c: Coincident(g0,g-3)
    c: Vertical(g0)
    c: Coincident(g1,g-3)
    c: Vertical(g1)
    c: Coincident(g2,g1)
    c: Coincident(g2,g0)
    c: DistanceX(g-3,g-3) = 2.2
    c: Diameter(g2) = 2.2
    c: DistanceY(g0,g2) = 1.15
    c: Coincident(g3,g0)
    c: Coincident(g3,g1)
    c: DistanceY(g0,g2) = 0
FEATURE [PartDesign::Pocket] Pocket028
  BaseFeature = -> Pad030
  Direction = (0,-1,2e-16)
  Length = 2
  Length2 = 5
  Profile = -> Sketch058
  ReferenceAxis = -> Sketch058 [N_Axis]
  Refine = true
  Suppressed = false
  Type = 0
FEATURE [Sketcher::SketchObject] Sketch059
  ArcFitTolerance = 1e-06
  AttachmentSupport = -> [Pocket028]
  ExternalGeometry = -> [Pocket028]
  FullyConstrained = true
  MakeInternals = false
  MapMode = 5
  Placement = pos=(0,0,6.8) rot=(0,0,1;0rad)
  sketch-geometry (3):
    g0: ArcOfCircle CenterX=-1.75 CenterY=-5.3 CenterZ=0 NormalX=0 NormalY=0 NormalZ=1 AngleXU=0 Radius=1 StartAngle=1.5708 EndAngle=3.14159
    g1: LineSegment StartX=-1.75 StartY=-4.3 StartZ=0 EndX=-1.75 EndY=-5.3 EndZ=0
    g2: LineSegment StartX=-2.75 StartY=-5.3 StartZ=0 EndX=-1.75 EndY=-5.3 EndZ=0
  constraints (8):
    c: PointOnObject(g0,g-3)
    c: Coincident(g0,g-3)
    c: Diameter(g0) = 2
    c: PointOnObject(g0,g-4)
    c: Coincident(g1,g0)
    c: Coincident(g1,g0)
    c: Coincident(g2,g0)
    c: Coincident(g2,g0)
FEATURE [PartDesign::Pad] Pad031
  BaseFeature = -> Pocket028
  Direction = (0,0,1)
  Length = 6
  Length2 = 10
  Profile = -> Sketch059
  ReferenceAxis = -> Sketch059 [N_Axis]
  Refine = true
  Suppressed = false
  Type = 0
FEATURE [Sketcher::SketchObject] Sketch060
  ArcFitTolerance = 1e-06
  AttachmentSupport = -> [Pad031]
  ExternalGeometry = -> [Pad031]
  FullyConstrained = true
  MakeInternals = false
  MapMode = 5
  Placement = pos=(10.3,0,0) rot=(0.57735,0.57735,0.57735;2.0944rad)
  sketch-geometry (8):
    g0: LineSegment StartX=-18.5 StartY=10.1 StartZ=0 EndX=-5.3 EndY=10.1 EndZ=0
    g1: LineSegment StartX=-5.3 StartY=10.1 StartZ=0 EndX=-5.3 EndY=1.6 EndZ=0
    g2: LineSegment StartX=-18.5 StartY=10.1 StartZ=0 EndX=-11.82 EndY=1.6 EndZ=0
    g3: LineSegment StartX=-11.82 StartY=1.6 StartZ=0 EndX=-5.3 EndY=1.6 EndZ=0
    g4: LineSegment StartX=5.3 StartY=10.1 StartZ=0 EndX=18.5 EndY=10.1 EndZ=0
    g5: LineSegment StartX=18.5 StartY=10.1 StartZ=0 EndX=11.82 EndY=1.6 EndZ=0
    g6: LineSegment StartX=5.3 StartY=10.1 StartZ=0 EndX=5.3 EndY=1.6 EndZ=0
    g7: LineSegment StartX=5.3 StartY=1.6 StartZ=0 EndX=11.82 EndY=1.6 EndZ=0
  constraints (20):
    c: Coincident(g0,g-3)
    c: Coincident(g0,g-3)
    c: Coincident(g1,g0)
    c: Vertical(g1)
    c: Coincident(g2,g0)
    c: Coincident(g3,g2)
    c: Coincident(g3,g1)
    c: Horizontal(g3)
    c: Coincident(g4,g-4)
    c: Coincident(g4,g-4)
    c: Coincident(g5,g4)
    c: Coincident(g6,g4)
    c: Vertical(g6)
    c: Coincident(g7,g6)
    c: Coincident(g7,g5)
    c: Horizontal(g7)
    c: DistanceY(g1,g1) = 8.5
    c: DistanceX(g3,g3) = 6.52
    c: DistanceX(g7,g7) = 6.52
    c: DistanceY(g6,g6) = 8.5
FEATURE [PartDesign::Pad] Pad032
  BaseFeature = -> Pad031
  Direction = (1,0,0)
  Length = 1.5
  Length2 = 10
  Profile = -> Sketch060
  ReferenceAxis = -> Sketch060 [N_Axis]
  Refine = true
  Reversed = true
  Suppressed = false
  Type = 0
FEATURE [Sketcher::SketchObject] Sketch061
  ArcFitTolerance = 1e-06
  AttachmentSupport = -> [Pad032]
  ExternalGeometry = -> [Pad032]
  FullyConstrained = true
  MakeInternals = false
  MapMode = 5
  Placement = pos=(0,0,1.6) rot=(1,0,0;3.14159rad)
  sketch-geometry (8):
    g0: LineSegment StartX=8.8 StartY=13 StartZ=0 EndX=16.4 EndY=13 EndZ=0
    g1: LineSegment StartX=16.4 StartY=13 StartZ=0 EndX=16.4 EndY=-13 EndZ=0
    g2: LineSegment StartX=16.4 StartY=-13 StartZ=0 EndX=8.8 EndY=-13 EndZ=0
    g3: LineSegment StartX=8.8 StartY=-13 StartZ=0 EndX=8.8 EndY=-5.3 EndZ=0
    g4: LineSegment StartX=8.8 StartY=-5.3 StartZ=0 EndX=12.7 EndY=-5.3 EndZ=0
    g5: LineSegment StartX=12.7 StartY=-5.3 StartZ=0 EndX=12.7 EndY=5.3 EndZ=0
    g6: LineSegment StartX=12.7 StartY=5.3 StartZ=0 EndX=8.8 EndY=5.3 EndZ=0
    g7: LineSegment StartX=8.8 StartY=5.3 StartZ=0 EndX=8.8 EndY=13 EndZ=0
  constraints (22):
    c: Coincident(g1,g0)
    c: Coincident(g2,g1)
    c: Coincident(g3,g2)
    c: Vertical(g3)
    c: Coincident(g4,g3)
    c: Horizontal(g4)
    c: Coincident(g5,g4)
    c: Coincident(g6,g5)
    c: Coincident(g7,g6)
    c: Coincident(g7,g0)
    c: Vertical(g7)
    c: Vertical(g1)
    c: Vertical(g5)
    c: Horizontal(g6)
    c: Coincident(g3,g-4)
    c: Coincident(g6,g-3)
    c: Horizontal(g0)
    c: Horizontal(g2)
    c: DistanceY(g1,g1) = 26
    c: DistanceX(g0,g0) = 7.6
    c: DistanceY(g-1,g0) = 13
    c: DistanceX(g5,g0) = 3.7
FEATURE [PartDesign::Pad] Pad033
  BaseFeature = -> Pad032
  Direction = (0,0,-1)
  Length = 1.5
  Length2 = 10
  Profile = -> Sketch061
  ReferenceAxis = -> Sketch061 [N_Axis]
  Refine = true
  Reversed = true
  Suppressed = false
  Type = 0
FEATURE [Sketcher::SketchObject] Sketch062
  ArcFitTolerance = 1e-06
  AttachmentSupport = -> [Pad033]
  ExternalGeometry = -> [Pad033]
  FullyConstrained = true
  MakeInternals = false
  MapMode = 5
  Placement = pos=(0,0,1.6) rot=(1,0,0;3.14159rad)
  sketch-geometry (8):
    g0: LineSegment StartX=8.8 StartY=13 StartZ=0 EndX=16.4 EndY=13 EndZ=0
    g1: LineSegment StartX=16.4 StartY=13 StartZ=0 EndX=16.4 EndY=-13 EndZ=0
    g2: LineSegment StartX=16.4 StartY=-13 StartZ=0 EndX=8.8 EndY=-13 EndZ=0
    g3: LineSegment StartX=8.8 StartY=-13 StartZ=0 EndX=8.8 EndY=-11.5 EndZ=0
    g4: LineSegment StartX=8.8 StartY=-11.5 StartZ=0 EndX=14.9 EndY=-11.5 EndZ=0
    g5: LineSegment StartX=14.9 StartY=-11.5 StartZ=0 EndX=14.9 EndY=11.5 EndZ=0
    g6: LineSegment StartX=14.9 StartY=11.5 StartZ=0 EndX=8.8 EndY=11.5 EndZ=0
    g7: LineSegment StartX=8.8 StartY=11.5 StartZ=0 EndX=8.8 EndY=13 EndZ=0
  constraints (20):
    c: Coincident(g0,g-3)
    c: Coincident(g0,g-4)
    c: Coincident(g1,g0)
    c: Coincident(g1,g-5)
    c: Coincident(g2,g1)
    c: Coincident(g2,g-5)
    c: Coincident(g3,g2)
    c: Vertical(g3)
    c: Coincident(g4,g3)
    c: Horizontal(g4)
    c: Coincident(g5,g4)
    c: Vertical(g5)
    c: Coincident(g6,g5)
    c: Horizontal(g6)
    c: Coincident(g7,g6)
    c: Coincident(g7,g0)
    c: Vertical(g7)
    c: DistanceY(g7,g7) = 1.5
    c: DistanceY(g3,g3) = 1.5
    c: DistanceX(g4,g1) = 1.5
FEATURE [PartDesign::Body] Body001  label="Upper_Torso"
  AllowCompound = false
  Group = -> [Binder,Sketch039,Pad021,Sketch040,Pocket021,Sketch043,Pocket022,Sketch044,Pocket023,Sketch045,Pad022,Sketch046,Pocket024,Sketch047,Pocket025,Sketch048,Pocket026,Sketch049,Pad023,Sketch050,Pad024,Sketch051,Pad025,Sketch052,Pad026,Sketch053,Pad027,Sketch054,Pocket027,Sketch055,Pad028,Sketch056,Pad029,Sketch057,Pad030,Sketch058,Pocket028,Sketch059,Pad031,Sketch060,Pad032,Sketch061,Pad033,Sketch062,+61 more]
  Origin = -> Origin001
  Tip = -> Pad251
COMPONENT P2 — recipe-attached ("Right_Leg", modeled in this document).
Construction recipe (the document's own serialized feature program — sketch geometry with constraints, then the solid features built on it; lengths are millimeters unless a unit is written):

FEATURE [PartDesign::SubShapeBinder] Binder001
  BindCopyOnChange = 0
  BindMode = 2
  ClaimChildren = false
  Context = -> Body002 [Binder001.]
  Fuse = false
  MakeFace = true
  OffsetFill = false
  OffsetIntersection = false
  OffsetJoinType = 0
  OffsetOpenResult = false
  PartialLoad = false
  Refine = true
  Relative = true
  _Version = 2
FEATURE [Sketcher::SketchObject] Sketch082
  ArcFitTolerance = 1e-06
  AttachmentSupport = -> [Binder001]
  ExternalGeometry = -> [Binder001]
  FullyConstrained = true
  MakeInternals = false
  MapMode = 5
  Placement = pos=(0,-7.1,0) rot=(1,0,0;1.5708rad)
  sketch-geometry (6):
    g0: ArcOfCircle CenterX=-23.6 CenterY=7.5 CenterZ=0 NormalX=0 NormalY=0 NormalZ=1 AngleXU=0 Radius=2.5 StartAngle=1.5708 EndAngle=4.71239
    g1: LineSegment StartX=-23.6 StartY=10 StartZ=0 EndX=-19.1 EndY=10 EndZ=0
    g2: LineSegment StartX=-19.1 StartY=10 StartZ=0 EndX=-19.1 EndY=2.1 EndZ=0
    g3: LineSegment StartX=-19.1 StartY=2.1 StartZ=0 EndX=-22.1 EndY=2.1 EndZ=0
    g4: LineSegment StartX=-22.1 StartY=2.1 StartZ=0 EndX=-22.1 EndY=5 EndZ=0
    g5: LineSegment StartX=-22.1 StartY=5 StartZ=0 EndX=-23.6 EndY=5 EndZ=0
  constraints (18):
    c: PointOnObject(g0,g-4)
    c: Coincident(g0,g-4)
    c: DistanceX(g0,g0) = 0
    c: DistanceX(g0,g0) = 0
    c: Coincident(g1,g0)
    c: Horizontal(g1)
    c: Coincident(g2,g1)
    c: Vertical(g2)
    c: Coincident(g3,g2)
    c: Horizontal(g3)
    c: Coincident(g4,g3)
    c: Vertical(g4)
    c: Coincident(g5,g4)
    c: Coincident(g5,g0)
    c: Horizontal(g5)
    c: DistanceX(g3,g3) = 3
    c: DistanceY(g2,g2) = 7.9
    c: DistanceX(g5,g5) = 1.5
FEATURE [PartDesign::Pad] Pad046
  Direction = (0,-1,2e-16)
  Length = 5.1
  Length2 = 10
  Profile = -> Sketch082
  ReferenceAxis = -> Sketch082 [N_Axis]
  Refine = true
  Suppressed = false
  Type = 0
FEATURE [Sketcher::SketchObject] Sketch083
  ArcFitTolerance = 1e-06
  AttachmentSupport = -> [Pad046]
  ExternalGeometry = -> [Pad046]
  FullyConstrained = true
  MakeInternals = false
  MapMode = 5
  Placement = pos=(0,-7.1,1.6e-15) rot=(0,0.707107,0.707107;3.14159rad)
  sketch-geometry (6):
    g0: LineSegment StartX=19.1 StartY=10 StartZ=0 EndX=19.1 EndY=2.1 EndZ=0
    g1: LineSegment StartX=19.1 StartY=2.1 StartZ=0 EndX=22.1 EndY=2.1 EndZ=0
    g2: LineSegment StartX=22.1 StartY=2.1 StartZ=0 EndX=22.1 EndY=5 EndZ=0
    g3: LineSegment StartX=22.1 StartY=5 StartZ=0 EndX=20.6 EndY=5 EndZ=0
    g4: LineSegment StartX=20.6 StartY=5 StartZ=0 EndX=20.6 EndY=10 EndZ=0
    g5: LineSegment StartX=20.6 StartY=10 StartZ=0 EndX=19.1 EndY=10 EndZ=0
  constraints (15):
    c: Coincident(g0,g-6)
    c: Coincident(g0,g-5)
    c: Coincident(g1,g0)
    c: Coincident(g1,g-4)
    c: PointOnObject(g2,g1)
    c: Coincident(g2,g-3)
    c: Vertical(g2)
    c: Coincident(g3,g2)
    c: Horizontal(g3)
    c: PointOnObject(g4,g-6)
    c: Coincident(g5,g4)
    c: Coincident(g5,g0)
    c: Coincident(g3,g4)
    c: DistanceX(g5,g5) = 1.5
    c: Vertical(g4)
FEATURE [PartDesign::Pad] Pad047
  BaseFeature = -> Pad046
  Direction = (0,1,-2e-16)
  Length = 3
  Length2 = 10
  Profile = -> Sketch083
  ReferenceAxis = -> Sketch083 [N_Axis]
  Refine = true
  Suppressed = false
  Type = 0
FEATURE [Sketcher::SketchObject] Sketch084
  ArcFitTolerance = 1e-06
  AttachmentSupport = -> [Pad047]
  ExternalGeometry = -> [Pad047]
  FullyConstrained = true
  MakeInternals = false
  MapMode = 5
  Placement = pos=(0,-12.2,2.8e-15) rot=(1,0,0;1.5708rad)
  sketch-geometry (1):
    g0: Circle CenterX=-23.6 CenterY=7.5 CenterZ=0 NormalX=0 NormalY=0 NormalZ=1 AngleXU=0 Radius=0.75
  constraints (2):
    c: Coincident(g0,g-3)
    c: Diameter(g0) = 1.5
FEATURE [PartDesign::Pocket] Pocket037
  BaseFeature = -> Pad047
  Direction = (0,1,-2e-16)
  Length = 6
  Length2 = 5
  Profile = -> Sketch084
  ReferenceAxis = -> Sketch084 [N_Axis]
  Refine = true
  Suppressed = false
  Type = 0
FEATURE [Sketcher::SketchObject] Sketch085
  ArcFitTolerance = 1e-06
  AttachmentSupport = -> [Pocket037]
  ExternalGeometry = -> [Pocket037]
  FullyConstrained = true
  MakeInternals = false
  MapMode = 5
  Placement = pos=(0,-12.2,2.8e-15) rot=(1,0,0;1.5708rad)
  sketch-geometry (8):
    g0: LineSegment StartX=-10.77 StartY=2.1 StartZ=0 EndX=-10.77 EndY=7.75 EndZ=0
    g1: ArcOfCircle CenterX=-10.77 CenterY=8.875 CenterZ=0 NormalX=0 NormalY=0 NormalZ=1 AngleXU=0 Radius=1.125 StartAngle=1.5708 EndAngle=4.71239
    g2: LineSegment StartX=-10.77 StartY=10 StartZ=0 EndX=-9.17 EndY=10 EndZ=0
    g3: ArcOfCircle CenterX=-9.17 CenterY=9.35 CenterZ=0 NormalX=0 NormalY=0 NormalZ=1 AngleXU=0 Radius=0.65 StartAngle=4.71239 EndAngle=7.85398
    g4: LineSegment StartX=-9.17 StartY=8.7 StartZ=0 EndX=-9.17 EndY=1.1 EndZ=0
    g5: LineSegment StartX=-9.17 StartY=1.1 StartZ=0 EndX=-21.1 EndY=1.1 EndZ=0
    g6: LineSegment StartX=-21.1 StartY=1.1 StartZ=0 EndX=-21.1 EndY=2.1 EndZ=0
    g7: LineSegment StartX=-21.1 StartY=2.1 StartZ=0 EndX=-10.77 EndY=2.1 EndZ=0
  constraints (27):
    c: Coincident(g1,g0)
    c: Coincident(g2,g1)
    c: Horizontal(g2)
    c: Coincident(g3,g2)
    c: Coincident(g4,g3)
    c: Vertical(g4)
    c: Coincident(g5,g4)
    c: Horizontal(g5)
    c: Coincident(g6,g5)
    c: DistanceY(g6,g6) = 1
    c: Vertical(g0)
    c: DistanceX(g-3,g0) = 8.33
    c: Diameter(g1) = 2.25
    c: DistanceX(g1,g0) = 0
    c: DistanceX(g1,g1) = 0
    c: DistanceX(g2,g2) = 1.6
    c: Diameter(g3) = 1.3
    c: DistanceX(g3,g2) = 0
    c: DistanceX(g3,g3) = 0
    c: DistanceY(g-4,g-4) = 7.9
    c: DistanceY(g0,g1) = 7.9
    c: Vertical(g6)
    c: DistanceX(g-3,g6) = 1
    c: Coincident(g7,g6)
    c: Coincident(g7,g0)
    c: Horizontal(g7)
    c: PointOnObject(g6,g-3)
FEATURE [PartDesign::Pad] Pad048
  BaseFeature = -> Pocket037
  Direction = (0,-1,2e-16)
  Length = 8.1
  Length2 = 10
  Profile = -> Sketch085
  ReferenceAxis = -> Sketch085 [N_Axis]
  Refine = true
  Reversed = true
  Suppressed = false
  Type = 0
FEATURE [Sketcher::SketchObject] Sketch086
  ArcFitTolerance = 1e-06
  AttachmentSupport = -> [Pad048]
  ExternalGeometry = -> [Pad048]
  FullyConstrained = true
  MakeInternals = false
  MapMode = 5
  Placement = pos=(0,5e-16,2.1) rot=(0,0,1;0rad)
  sketch-geometry (4):
    g0: LineSegment StartX=-19.1 StartY=-4.1 StartZ=0 EndX=-19.1 EndY=-10.2 EndZ=0
    g1: LineSegment StartX=-19.1 StartY=-10.2 StartZ=0 EndX=-10.77 EndY=-10.2 EndZ=0
    g2: LineSegment StartX=-10.77 StartY=-10.2 StartZ=0 EndX=-10.77 EndY=-4.1 EndZ=0
    g3: LineSegment StartX=-10.77 StartY=-4.1 StartZ=0 EndX=-19.1 EndY=-4.1 EndZ=0
  constraints (11):
    c: Coincident(g0,g1)
    c: Coincident(g1,g2)
    c: Coincident(g2,g3)
    c: Coincident(g3,g0)
    c: Vertical(g0)
    c: Vertical(g2)
    c: Horizontal(g1)
    c: Horizontal(g3)
    c: PointOnObject(g1,g-4)
    c: DistanceY(g-6,g1) = 2
    c: Coincident(g0,g-5)
FEATURE [PartDesign::Pocket] Pocket038
  BaseFeature = -> Pad048
  Direction = (0,0,-1)
  Length = 5
  Length2 = 5
  Profile = -> Sketch086
  ReferenceAxis = -> Sketch086 [N_Axis]
  Refine = true
  Suppressed = false
  Type = 0
FEATURE [Sketcher::SketchObject] Sketch087
  ArcFitTolerance = 1e-06
  AttachmentSupport = -> [Pocket038]
  ExternalGeometry = -> [Pocket038]
  FullyConstrained = true
  MakeInternals = false
  MapMode = 5
  Placement = pos=(0,-12.2,0) rot=(1,0,0;1.5708rad)
  sketch-geometry (4):
    g0: ArcOfCircle CenterX=-10.77 CenterY=8.875 CenterZ=0 NormalX=0 NormalY=0 NormalZ=1 AngleXU=0 Radius=1.125 StartAngle=1.5708 EndAngle=4.71239
    g1: ArcOfCircle CenterX=-9.17 CenterY=9.35 CenterZ=0 NormalX=0 NormalY=0 NormalZ=1 AngleXU=0 Radius=0.65 StartAngle=4.71239 EndAngle=7.85398
    g2: LineSegment StartX=-10.77 StartY=10 StartZ=0 EndX=-10.77 EndY=7.75 EndZ=0
    g3: LineSegment StartX=-9.17 StartY=10 StartZ=0 EndX=-9.17 EndY=8.7 EndZ=0
  constraints (8):
    c: Tangent(g0,g-4) = -1.5708
    c: Coincident(g0,g-4)
    c: Tangent(g1,g-3) = -1.5708
    c: Coincident(g1,g-3)
    c: Coincident(g2,g0)
    c: Coincident(g2,g0)
    c: Coincident(g3,g1)
    c: Coincident(g3,g1)
FEATURE [PartDesign::Pocket] Pocket039
  BaseFeature = -> Pocket038
  Direction = (0,1,-2e-16)
  Length = 2
  Length2 = 5
  Profile = -> Sketch087
  ReferenceAxis = -> Sketch087 [N_Axis]
  Refine = true
  Suppressed = false
  Type = 0
FEATURE [PartDesign::Fillet] Fillet002
  Base = -> Pocket039 [Edge38,Edge37]
  BaseFeature = -> Pocket039
  Radius = 0.5
  Refine = true
  SupportTransform = false
  Suppressed = false
  UseAllEdges = false
FEATURE [Sketcher::SketchObject] Sketch088
  ArcFitTolerance = 1e-06
  AttachmentSupport = -> [Fillet002]
  ExternalGeometry = -> [Fillet002]
  FullyConstrained = true
  MakeInternals = false
  MapMode = 5
  Placement = pos=(0,-12.2,0) rot=(1,0,0;1.5708rad)
  sketch-geometry (4):
    g0: LineSegment StartX=-10.77 StartY=2.1 StartZ=0 EndX=-10.77 EndY=3.1 EndZ=0
    g1: LineSegment StartX=-10.77 StartY=3.1 StartZ=0 EndX=-19.1 EndY=3.1 EndZ=0
    g2: LineSegment StartX=-19.1 StartY=3.1 StartZ=0 EndX=-19.1 EndY=2.1 EndZ=0
    g3: LineSegment StartX=-19.1 StartY=2.1 StartZ=0 EndX=-10.77 EndY=2.1 EndZ=0
  constraints (11):
    c: Coincident(g0,g1)
    c: Coincident(g1,g2)
    c: Coincident(g2,g3)
    c: Coincident(g3,g0)
    c: Vertical(g0)
    c: Vertical(g2)
    c: Horizontal(g1)
    c: Horizontal(g3)
    c: Coincident(g0,g-5)
    c: PointOnObject(g1,g-4)
    c: DistanceY(g2,g2) = 1
FEATURE [PartDesign::Pad] Pad049
  BaseFeature = -> Fillet002
  Direction = (0,-1,2e-16)
  Length = 2
  Length2 = 10
  Profile = -> Sketch088
  ReferenceAxis = -> Sketch088 [N_Axis]
  Refine = true
  Reversed = true
  Suppressed = false
  Type = 0
FEATURE [Sketcher::SketchObject] Sketch089
  ArcFitTolerance = 1e-06
  AttachmentSupport = -> [Pad049]
  ExternalGeometry = -> [Pad049]
  FullyConstrained = true
  MakeInternals = false
  MapMode = 5
  Placement = pos=(0,-12.2,0) rot=(1,0,0;1.5708rad)
  sketch-geometry (4):
    g0: LineSegment StartX=-21.1 StartY=2.1 StartZ=0 EndX=-21.1 EndY=1.1 EndZ=0
    g1: LineSegment StartX=-21.1 StartY=1.1 StartZ=0 EndX=-9.17 EndY=1.1 EndZ=0
    g2: LineSegment StartX=-9.17 StartY=1.1 StartZ=0 EndX=-9.17 EndY=2.1 EndZ=0
    g3: LineSegment StartX=-9.17 StartY=2.1 StartZ=0 EndX=-21.1 EndY=2.1 EndZ=0
  constraints (10):
    c: Coincident(g0,g1)
    c: Coincident(g1,g2)
    c: Coincident(g2,g3)
    c: Coincident(g3,g0)
    c: Vertical(g0)
    c: Vertical(g2)
    c: Horizontal(g1)
    c: Horizontal(g3)
    c: Coincident(g0,g-3)
    c: Coincident(g1,g-5)
FEATURE [PartDesign::Pocket] Pocket040
  BaseFeature = -> Pad049
  Direction = (0,1,-2e-16)
  Length = 9
  Length2 = 5
  Profile = -> Sketch089
  ReferenceAxis = -> Sketch089 [N_Axis]
  Refine = true
  Suppressed = false
  Type = 0
FEATURE [Sketcher::SketchObject] Sketch090
  ArcFitTolerance = 1e-06
  AttachmentOffset = pos=(0,0,-1) rot=(0,0,1;0rad)
  AttachmentSupport = -> [Pocket040]
  ExternalGeometry = -> [Pocket040]
  FullyConstrained = true
  MakeInternals = false
  MapMode = 5
  Placement = pos=(-21.1,0,0) rot=(0.57735,-0.57735,-0.57735;2.0944rad)
  sketch-geometry (16):
    g0: LineSegment StartX=12.2 StartY=2.1 StartZ=0 EndX=11 EndY=-5.15 EndZ=0
    g1: LineSegment StartX=4 StartY=-24.9 StartZ=0 EndX=6.5 EndY=-24.9 EndZ=0
    g2: LineSegment StartX=6.5 StartY=-24.9 StartZ=0 EndX=6.5 EndY=-35.4 EndZ=0
    g3: LineSegment StartX=6.5 StartY=-35.4 StartZ=0 EndX=10 EndY=-35.4 EndZ=0
    g4: LineSegment StartX=10 StartY=-35.4 StartZ=0 EndX=10 EndY=-22.8 EndZ=0
    g5: LineSegment StartX=10 StartY=-22.8 StartZ=0 EndX=9.5 EndY=-22.8 EndZ=0
    g6: LineSegment StartX=9.5 StartY=-22.8 StartZ=0 EndX=9.5 EndY=-11.9 EndZ=0
    g7: LineSegment StartX=9.5 StartY=-11.9 StartZ=0 EndX=12 EndY=-11.9 EndZ=0
    g8: LineSegment StartX=12 StartY=-11.9 StartZ=0 EndX=12 EndY=-5.15 EndZ=0
    g9: LineSegment StartX=12 StartY=-5.15 StartZ=0 EndX=11 EndY=-5.15 EndZ=0
    g10: LineSegment StartX=4.1 StartY=2.1 StartZ=0 EndX=4.1 EndY=-5.15 EndZ=0
    g11: LineSegment StartX=4.1 StartY=-5.15 StartZ=0 EndX=-1.8e-15 EndY=-5.15 EndZ=0
    g12: LineSegment StartX=-1.8e-15 StartY=-5.15 StartZ=0 EndX=-1.8e-15 EndY=-15.15 EndZ=0
    g13: LineSegment StartX=4 StartY=-24.9 StartZ=0 EndX=4 EndY=-15.15 EndZ=0
    g14: LineSegment StartX=4 StartY=-15.15 StartZ=0 EndX=-1.8e-15 EndY=-15.15 EndZ=0
    g15: LineSegment StartX=4.1 StartY=2.1 StartZ=0 EndX=12.2 EndY=2.1 EndZ=0
  constraints (47):
    c: Coincident(g0,g-3)
    c: Horizontal(g1)
    c: Coincident(g2,g1)
    c: Vertical(g2)
    c: Coincident(g3,g2)
    c: Horizontal(g3)
    c: Coincident(g4,g3)
    c: Vertical(g4)
    c: Coincident(g5,g4)
    c: Horizontal(g5)
    c: Coincident(g6,g5)
    c: Vertical(g6)
    c: Coincident(g7,g6)
    c: Horizontal(g7)
    c: Coincident(g8,g7)
    c: Vertical(g8)
    c: Coincident(g9,g8)
    c: Coincident(g9,g0)
    c: Horizontal(g9)
    c: DistanceX(g1,g6) = 5.5
    c: DistanceY(g8,g8) = 6.75
    c: DistanceY(g8,g0) = 7.25
    c: DistanceX(g9,g9) = 1
    c: Coincident(g10,g-3)
    c: Vertical(g10)
    c: Coincident(g11,g10)
    c: Horizontal(g11)
    c: Coincident(g12,g11)
    c: Vertical(g12)
    c: Coincident(g13,g1)
    c: Vertical(g13)
    c: Coincident(g14,g13)
    c: Coincident(g14,g12)
    c: Horizontal(g14)
    c: DistanceX(g11,g8) = 12
    c: DistanceX(g7,g7) = 2.5
    c: DistanceY(g10,g10) = 7.25
    c: DistanceY(g12,g12) = 10
    c: DistanceX(g11,g11) = 4.1
    c: DistanceX(g1,g1) = 2.5
    c: DistanceY(g3,g-4) = 45.4
    c: DistanceY(g1,g-5) = 34.9
    c: DistanceX(g5,g5) = 0.5
    c: DistanceX(g3,g3) = 3.5
    c: DistanceY(g4,g4) = 12.6
    c: Coincident(g15,g10)
    c: Coincident(g15,g0)
FEATURE [PartDesign::Pad] Pad050
  BaseFeature = -> Pocket040
  Direction = (-1,0,0)
  Length = 1
  Length2 = 10
  Profile = -> Sketch090
  ReferenceAxis = -> Sketch090 [N_Axis]
  Refine = true
  Reversed = true
  Suppressed = false
  Type = 0
FEATURE [Sketcher::SketchObject] Sketch091
  ArcFitTolerance = 1e-06
  AttachmentSupport = -> [Pad050]
  ExternalGeometry = -> [Pad050]
  FullyConstrained = true
  MakeInternals = false
  MapMode = 5
  Placement = pos=(-20.1,0,0) rot=(0.57735,0.57735,0.57735;2.0944rad)
  sketch-geometry (4):
    g0: LineSegment StartX=-4.1 StartY=2.1 StartZ=0 EndX=-12.2 EndY=2.1 EndZ=0
    g1: LineSegment StartX=-12.2 StartY=2.1 StartZ=0 EndX=-11 EndY=-5.15 EndZ=0
    g2: LineSegment StartX=-11 StartY=-5.15 StartZ=0 EndX=-4.1 EndY=-5.15 EndZ=0
    g3: LineSegment StartX=-4.1 StartY=-5.15 StartZ=0 EndX=-4.1 EndY=2.1 EndZ=0
  constraints (8):
    c: Coincident(g0,g-3)
    c: Coincident(g0,g-4)
    c: Coincident(g1,g0)
    c: Coincident(g1,g-4)
    c: Coincident(g2,g1)
    c: Coincident(g2,g-3)
    c: Coincident(g3,g2)
    c: Coincident(g3,g0)
FEATURE [PartDesign::Pad] Pad051
  BaseFeature = -> Pad050
  Direction = (1,0,0)
  Length = 1
  Length2 = 10
  Profile = -> Sketch091
  ReferenceAxis = -> Sketch091 [N_Axis]
  Refine = true
  Suppressed = false
  Type = 0
FEATURE [Sketcher::SketchObject] Sketch092
  ArcFitTolerance = 1e-06
  AttachmentSupport = -> [Pad051]
  ExternalGeometry = -> [Pad051]
  FullyConstrained = true
  MakeInternals = false
  MapMode = 5
  Placement = pos=(-20.1,0,0) rot=(0.57735,0.57735,0.57735;2.0944rad)
  sketch-geometry (8):
    g0: LineSegment StartX=-4 StartY=-15.15 StartZ=0 EndX=-4 EndY=-24.9 EndZ=0
    g1: LineSegment StartX=-4 StartY=-24.9 StartZ=0 EndX=-6.5 EndY=-24.9 EndZ=0
    g2: LineSegment StartX=-6.5 StartY=-24.9 StartZ=0 EndX=-6.5 EndY=-35.4 EndZ=0
    g3: LineSegment StartX=-6.5 StartY=-35.4 StartZ=0 EndX=-10 EndY=-35.4 EndZ=0
    g4: LineSegment StartX=-10 StartY=-35.4 StartZ=0 EndX=-10 EndY=-22.8 EndZ=0
    g5: LineSegment StartX=-4 StartY=-15.15 StartZ=0 EndX=-9.5 EndY=-15.15 EndZ=0
    g6: LineSegment StartX=-9.5 StartY=-15.15 StartZ=0 EndX=-9.5 EndY=-22.8 EndZ=0
    g7: LineSegment StartX=-9.5 StartY=-22.8 StartZ=0 EndX=-10 EndY=-22.8 EndZ=0
  constraints (17):
    c: Coincident(g0,g-3)
    c: Coincident(g0,g-9)
    c: Coincident(g1,g0)
    c: Coincident(g1,g-9)
    c: Coincident(g2,g1)
    c: Coincident(g2,g-6)
    c: Coincident(g3,g2)
    c: Coincident(g3,g-7)
    c: Coincident(g4,g3)
    c: Coincident(g4,g-8)
    c: Coincident(g5,g0)
    c: PointOnObject(g5,g-4)
    c: Horizontal(g5)
    c: Coincident(g6,g5)
    c: Coincident(g6,g-8)
    c: Coincident(g7,g4)
    c: Coincident(g6,g7)
FEATURE [PartDesign::Pad] Pad052
  BaseFeature = -> Pad051
  Direction = (1,0,0)
  Length = 0.5
  Length2 = 10
  Profile = -> Sketch092
  ReferenceAxis = -> Sketch092 [N_Axis]
  Refine = true
  Suppressed = false
  Type = 0
FEATURE [Sketcher::SketchObject] Sketch093
  ArcFitTolerance = 1e-06
  AttachmentSupport = -> [Pad052]
  ExternalGeometry = -> [Pad052]
  FullyConstrained = true
  MakeInternals = false
  MapMode = 5
  Placement = pos=(0,1.8e-15,0) rot=(0,0.707107,0.707107;3.14159rad)
  sketch-geometry (8):
    g0: LineSegment StartX=20.1 StartY=-5.15 StartZ=0 EndX=7.6 EndY=-5.15 EndZ=0
    g1: LineSegment StartX=20.1 StartY=-15.15 StartZ=0 EndX=7.6 EndY=-15.15 EndZ=0
    g2: LineSegment StartX=7.6 StartY=-5.15 StartZ=0 EndX=7.6 EndY=-15.15 EndZ=0
    g3: LineSegment StartX=20.1 StartY=-15.15 StartZ=0 EndX=20.1 EndY=-13.55 EndZ=0
    g4: LineSegment StartX=20.1 StartY=-13.55 StartZ=0 EndX=8.6 EndY=-13.55 EndZ=0
    g5: LineSegment StartX=8.6 StartY=-13.55 StartZ=0 EndX=8.6 EndY=-6.75 EndZ=0
    g6: LineSegment StartX=8.6 StartY=-6.75 StartZ=0 EndX=20.1 EndY=-6.75 EndZ=0
    g7: LineSegment StartX=20.1 StartY=-6.75 StartZ=0 EndX=20.1 EndY=-5.15 EndZ=0
  constraints (23):
    c: Coincident(g0,g-5)
    c: Horizontal(g0)
    c: Coincident(g1,g-4)
    c: Horizontal(g1)
    c: Coincident(g2,g0)
    c: Coincident(g2,g1)
    c: Vertical(g2)
    c: DistanceY(g-6,g-6) = 10
    c: Coincident(g3,g1)
    c: Vertical(g3)
    c: Coincident(g4,g3)
    c: Horizontal(g4)
    c: Coincident(g5,g4)
    c: Vertical(g5)
    c: Coincident(g6,g5)
    c: Horizontal(g6)
    c: PointOnObject(g6,g-7)
    c: Coincident(g7,g6)
    c: Coincident(g7,g0)
    c: DistanceX(g0,g5) = 1
    c: DistanceY(g5,g0) = 1.6
    c: DistanceY(g1,g4) = 1.6
    c: DistanceX(g0,g6) = 12.5
FEATURE [PartDesign::Pad] Pad053
  BaseFeature = -> Pad052
  Direction = (0,1,-2e-16)
  Length = 4.1
  Length2 = 10
  Profile = -> Sketch093
  ReferenceAxis = -> Sketch093 [N_Axis]
  Refine = true
  Reversed = true
  Suppressed = false
  Type = 0
FEATURE [Sketcher::SketchObject] Sketch094
  ArcFitTolerance = 1e-06
  AttachmentSupport = -> [Pad053]
  ExternalGeometry = -> [Pad053]
  FullyConstrained = true
  MakeInternals = false
  MapMode = 5
  Placement = pos=(0,-12,0) rot=(1,0,0;1.5708rad)
  sketch-geometry (6):
    g0: LineSegment StartX=-20.1 StartY=-5.15 StartZ=0 EndX=-8.6 EndY=-5.15 EndZ=0
    g1: LineSegment StartX=-8.6 StartY=-5.15 StartZ=0 EndX=-8.6 EndY=-13.35 EndZ=0
    g2: LineSegment StartX=-20.1 StartY=-11.9 StartZ=0 EndX=-17.3 EndY=-11.9 EndZ=0
    g3: LineSegment StartX=-8.6 StartY=-13.35 StartZ=0 EndX=-14.6 EndY=-13.35 EndZ=0
    g4: ArcOfCircle CenterX=-14.6 CenterY=-10.1112 CenterZ=0 NormalX=0 NormalY=0 NormalZ=1 AngleXU=0 Radius=3.23879 StartAngle=3.72672 EndAngle=4.71239
    g5: LineSegment StartX=-20.1 StartY=-5.15 StartZ=0 EndX=-20.1 EndY=-11.9 EndZ=0
  constraints (20):
    c: DistanceX(g-4,g-4) = 1
    c: Coincident(g0,g-4)
    c: Horizontal(g0)
    c: DistanceX(g0,g0) = 11.5
    c: Coincident(g1,g0)
    c: Vertical(g1)
    c: DistanceY(g1,g1) = 8.2
    c: Coincident(g2,g-3)
    c: Horizontal(g2)
    c: Coincident(g3,g1)
    c: Horizontal(g3)
    c: Coincident(g4,g3)
    c: Coincident(g4,g2)
    c: DistanceX(g2,g2) = 2.8
    c: DistanceX(g4,g3) = 0
    c: DistanceX(g-5,g4) = 6.5
    c: DistanceX(g3,g1) = 6
    c: DistanceX(g2,g1) = 8.7
    c: Coincident(g5,g2)
    c: Coincident(g5,g0)
FEATURE [PartDesign::Pad] Pad054
  BaseFeature = -> Pad053
  Direction = (0,-1,2e-16)
  Length = 1.5
  Length2 = 10
  Profile = -> Sketch094
  ReferenceAxis = -> Sketch094 [N_Axis]
  Refine = true
  Reversed = true
  Suppressed = false
  Type = 0
FEATURE [Sketcher::SketchObject] Sketch095
  ArcFitTolerance = 1e-06
  AttachmentSupport = -> [Pad054]
  ExternalGeometry = -> [Pad054]
  FullyConstrained = true
  MakeInternals = false
  MapMode = 5
  Placement = pos=(-19.1,0,9.2e-15) rot=(0.57735,0.57735,0.57735;2.0944rad)
  sketch-geometry (4):
    g0: LineSegment StartX=-12.2 StartY=2.1 StartZ=0 EndX=-10.2 EndY=2.1 EndZ=0
    g1: LineSegment StartX=-12.2 StartY=2.1 StartZ=0 EndX=-11 EndY=-5.15 EndZ=0
    g2: LineSegment StartX=-11 StartY=-5.15 StartZ=0 EndX=-9 EndY=-5.15 EndZ=0
    g3: LineSegment StartX=-9 StartY=-5.15 StartZ=0 EndX=-10.2 EndY=2.1 EndZ=0
  constraints (10):
    c: DistanceX(g-4,g-4) = 2
    c: Coincident(g0,g-4)
    c: Coincident(g0,g-4)
    c: Coincident(g1,g0)
    c: Coincident(g1,g-5)
    c: Coincident(g2,g1)
    c: PointOnObject(g2,g-6)
    c: Coincident(g3,g2)
    c: Coincident(g3,g0)
    c: DistanceX(g2,g2) = 2
FEATURE [PartDesign::Pad] Pad055
  BaseFeature = -> Pad054
  Direction = (1,0,0)
  Length = 9.93
  Length2 = 10
  Profile = -> Sketch095
  ReferenceAxis = -> Sketch095 [N_Axis]
  Refine = true
  Suppressed = false
  Type = 0
FEATURE [Sketcher::SketchObject] Sketch096
  ArcFitTolerance = 1e-06
  AttachmentSupport = -> [Pad055]
  ExternalGeometry = -> [Pad055]
  FullyConstrained = true
  MakeInternals = false
  MapMode = 5
  Placement = pos=(0,-12.2,0) rot=(1,0,0;1.5708rad)
  sketch-geometry (3):
    g0: LineSegment StartX=-9.17 StartY=2.1 StartZ=0 EndX=-9.17 EndY=-5.15 EndZ=0
    g1: LineSegment StartX=-9.17 StartY=-5.15 StartZ=0 EndX=-10.1 EndY=-5.15 EndZ=0
    g2: LineSegment StartX=-10.1 StartY=-5.15 StartZ=0 EndX=-9.17 EndY=2.1 EndZ=0
  constraints (7):
    c: Coincident(g0,g-3)
    c: Coincident(g0,g-3)
    c: Coincident(g1,g0)
    c: PointOnObject(g1,g-4)
    c: Coincident(g2,g1)
    c: Coincident(g2,g0)
    c: DistanceX(g-4,g1) = 11
FEATURE [PartDesign::Pocket] Pocket041
  BaseFeature = -> Pad055
  Direction = (0,1,-2e-16)
  Length = 5
  Length2 = 5
  Profile = -> Sketch096
  ReferenceAxis = -> Sketch096 [N_Axis]
  Refine = true
  Suppressed = false
  Type = 0
FEATURE [Sketcher::SketchObject] Sketch097
  ArcFitTolerance = 1e-06
  AttachmentSupport = -> [Pocket041]
  ExternalGeometry = -> [Pocket041]
  FullyConstrained = true
  MakeInternals = false
  MapMode = 5
  Placement = pos=(0,-4.1,0) rot=(0,0.707107,0.707107;3.14159rad)
  sketch-geometry (4):
    g0: LineSegment StartX=9.17 StartY=2.1 StartZ=0 EndX=10.77 EndY=2.1 EndZ=0
    g1: LineSegment StartX=9.17 StartY=2.1 StartZ=0 EndX=10.1 EndY=-5.15 EndZ=0
    g2: LineSegment StartX=10.1 StartY=-5.15 StartZ=0 EndX=11.7 EndY=-5.15 EndZ=0
    g3: LineSegment StartX=11.7 StartY=-5.15 StartZ=0 EndX=10.77 EndY=2.1 EndZ=0
  constraints (9):
    c: Coincident(g0,g-4)
    c: Coincident(g0,g-3)
    c: Coincident(g1,g0)
    c: Coincident(g1,g-4)
    c: Coincident(g2,g1)
    c: PointOnObject(g2,g-5)
    c: Coincident(g3,g2)
    c: Coincident(g3,g0)
    c: DistanceX(g2,g2) = 1.6
FEATURE [PartDesign::Pad] Pad056
  BaseFeature = -> Pocket041
  Direction = (0,1,-2e-16)
  Length = 6.5
  Length2 = 10
  Profile = -> Sketch097
  ReferenceAxis = -> Sketch097 [N_Axis]
  Refine = true
  Reversed = true
  Suppressed = false
  Type = 0
FEATURE [Sketcher::SketchObject] Sketch098
  ArcFitTolerance = 1e-06
  AttachmentSupport = -> [Pad056]
  ExternalGeometry = -> [Pad056]
  FullyConstrained = true
  MakeInternals = false
  MapMode = 5
  Placement = pos=(-8.6,0,0) rot=(0.57735,0.57735,0.57735;2.0944rad)
  sketch-geometry (4):
    g0: LineSegment StartX=-10.5 StartY=-5.15 StartZ=0 EndX=-4.1 EndY=-5.15 EndZ=0
    g1: LineSegment StartX=-4.1 StartY=-5.15 StartZ=0 EndX=-4.1 EndY=-15.15 EndZ=0
    g2: LineSegment StartX=-4.1 StartY=-15.15 StartZ=0 EndX=-10.5 EndY=-13.35 EndZ=0
    g3: LineSegment StartX=-10.5 StartY=-13.35 StartZ=0 EndX=-10.5 EndY=-5.15 EndZ=0
  constraints (8):
    c: Coincident(g0,g-3)
    c: Coincident(g0,g-4)
    c: Coincident(g1,g0)
    c: Coincident(g1,g-4)
    c: Coincident(g2,g1)
    c: Coincident(g2,g-3)
    c: Coincident(g3,g2)
    c: Coincident(g3,g0)
FEATURE [PartDesign::Pad] Pad057
  BaseFeature = -> Pad056
  Direction = (1,0,0)
  Length = 1
  Length2 = 10
  Profile = -> Sketch098
  ReferenceAxis = -> Sketch098 [N_Axis]
  Refine = true
  Reversed = true
  Suppressed = false
  Type = 0
FEATURE [Sketcher::SketchObject] Sketch099
  ArcFitTolerance = 1e-06
  AttachmentSupport = -> [Pad057]
  ExternalGeometry = -> [Pad057]
  FullyConstrained = false
  MakeInternals = false
  MapMode = 5
  Placement = pos=(0,-4.1,0) rot=(0,0.707107,0.707107;3.14159rad)
  sketch-geometry (4):
    g0: LineSegment StartX=8.6 StartY=-6.7914 StartZ=0 EndX=8.6 EndY=-13.55 EndZ=0
    g1: LineSegment StartX=8.6 StartY=-13.55 StartZ=0 EndX=9.6 EndY=-13.55 EndZ=0
    g2: LineSegment StartX=9.6 StartY=-13.55 StartZ=0 EndX=9.6 EndY=-6.7914 EndZ=0
    g3: LineSegment StartX=9.6 StartY=-6.7914 StartZ=0 EndX=8.6 EndY=-6.7914 EndZ=0
  constraints (10):
    c: Coincident(g0,g1)
    c: Coincident(g1,g2)
    c: Coincident(g2,g3)
    c: Coincident(g3,g0)
    c: Vertical(g0)
    c: Vertical(g2)
    c: Horizontal(g1)
    c: Horizontal(g3)
    c: PointOnObject(g0,g-3)
    c: Coincident(g1,g-4)
FEATURE [PartDesign::Pad] Pad058
  BaseFeature = -> Pad057
  Direction = (0,1,-2e-16)
  Length = 1
  Length2 = 10
  Profile = -> Sketch099
  ReferenceAxis = -> Sketch099 [N_Axis]
  Refine = true
  Suppressed = false
  Type = 0
FEATURE [Sketcher::SketchObject] Sketch100
  ArcFitTolerance = 1e-06
  AttachmentSupport = -> [Pad058]
  ExternalGeometry = -> [Pad058]
  FullyConstrained = true
  MakeInternals = false
  MapMode = 5
  Placement = pos=(0,-4.1,0) rot=(1,0,0;1.5708rad)
  sketch-geometry (4):
    g0: LineSegment StartX=-9.6 StartY=-5.15 StartZ=0 EndX=-20.1 EndY=-5.15 EndZ=0
    g1: LineSegment StartX=-20.1 StartY=-5.15 StartZ=0 EndX=-20.1 EndY=-6.75 EndZ=0
    g2: LineSegment StartX=-20.1 StartY=-6.75 StartZ=0 EndX=-9.6 EndY=-6.75 EndZ=0
    g3: LineSegment StartX=-9.6 StartY=-6.75 StartZ=0 EndX=-9.6 EndY=-5.15 EndZ=0
  constraints (10):
    c: Coincident(g0,g1)
    c: Coincident(g1,g2)
    c: Coincident(g2,g3)
    c: Coincident(g3,g0)
    c: Horizontal(g0)
    c: Horizontal(g2)
    c: Vertical(g1)
    c: Vertical(g3)
    c: Coincident(g0,g-6)
    c: Coincident(g1,g-5)
FEATURE [PartDesign::Pad] Pad059
  BaseFeature = -> Pad058
  Direction = (0,-1,2e-16)
  Length = 7
  Length2 = 10
  Profile = -> Sketch100
  ReferenceAxis = -> Sketch100 [N_Axis]
  Refine = true
  Suppressed = false
  Type = 0
FEATURE [Sketcher::SketchObject] Sketch101
  ArcFitTolerance = 1e-06
  AttachmentSupport = -> [Pad059]
  ExternalGeometry = -> [Pad059]
  FullyConstrained = true
  MakeInternals = false
  MapMode = 5
  Placement = pos=(0,-10.5,0) rot=(0,0.707107,0.707107;3.14159rad)
  sketch-geometry (8):
    g0: LineSegment StartX=9.6 StartY=-13.35 StartZ=0 EndX=14.6 EndY=-13.35 EndZ=0
    g1: ArcOfCircle CenterX=14.6 CenterY=-10.1112 CenterZ=0 NormalX=0 NormalY=0 NormalZ=1 AngleXU=0 Radius=3.23879 StartAngle=4.71239 EndAngle=5.69806
    g2: LineSegment StartX=17.3 StartY=-11.9 StartZ=0 EndX=20.1 EndY=-11.9 EndZ=0
    g3: LineSegment StartX=20.1 StartY=-11.9 StartZ=0 EndX=20.1 EndY=-10.4 EndZ=0
    g4: LineSegment StartX=20.1 StartY=-10.4 StartZ=0 EndX=16.3146 EndY=-10.4 EndZ=0
    g5: LineSegment StartX=9.6 StartY=-13.35 StartZ=0 EndX=9.6 EndY=-11.85 EndZ=0
    g6: LineSegment StartX=9.6 StartY=-11.85 StartZ=0 EndX=14.6 EndY=-11.85 EndZ=0
    g7: ArcOfCircle CenterX=14.6 CenterY=-10.1112 CenterZ=0 NormalX=0 NormalY=0 NormalZ=1 AngleXU=0 Radius=1.73879 StartAngle=4.71239 EndAngle=6.11632
  constraints (22):
    c: Coincident(g0,g-7)
    c: Coincident(g1,g0)
    c: Tangent(g1,g-5) = -1.5708
    c: PointOnObject(g2,g-5)
    c: Coincident(g2,g-4)
    c: Horizontal(g2)
    c: PointOnObject(g3,g2)
    c: PointOnObject(g3,g-3)
    c: Vertical(g3)
    c: Coincident(g4,g3)
    c: Horizontal(g4)
    c: Coincident(g0,g-6)
    c: Coincident(g5,g0)
    c: PointOnObject(g5,g-7)
    c: Coincident(g6,g5)
    c: Horizontal(g6)
    c: Coincident(g7,g6)
    c: Coincident(g7,g4)
    c: Coincident(g7,g1)
    c: DistanceY(g3,g3) = 1.5
    c: DistanceY(g5,g5) = 1.5
    c: DistanceX(g6,g0) = 0
FEATURE [PartDesign::Pad] Pad060
  BaseFeature = -> Pad059
  Direction = (0,1,-2e-16)
  Length = 1
  Length2 = 10
  Profile = -> Sketch101
  ReferenceAxis = -> Sketch101 [N_Axis]
  Refine = true
  Suppressed = false
  Type = 0
FEATURE [Sketcher::SketchObject] Sketch102
  ArcFitTolerance = 1e-06
  AttachmentSupport = -> [Pad060]
  ExternalGeometry = -> [Pad060]
  FullyConstrained = true
  MakeInternals = false
  MapMode = 5
  Placement = pos=(-9.9e-15,-9.5,0) rot=(1,0,0;1.5708rad)
  sketch-geometry (8):
    g0: LineSegment StartX=-19.6 StartY=-22.8 StartZ=0 EndX=-19.6 EndY=-15.15 EndZ=0
    g1: LineSegment StartX=-19.6 StartY=-15.15 StartZ=0 EndX=-20.1 EndY=-15.15 EndZ=0
    g2: LineSegment StartX=-20.1 StartY=-15.15 StartZ=0 EndX=-20.1 EndY=-10.4 EndZ=0
    g3: LineSegment StartX=-20.1 StartY=-10.4 StartZ=0 EndX=-16.3146 EndY=-10.4 EndZ=0
    g4: ArcOfCircle CenterX=-14.6 CenterY=-10.1112 CenterZ=0 NormalX=0 NormalY=0 NormalZ=1 AngleXU=0 Radius=1.73879 StartAngle=3.30845 EndAngle=4.71239
    g5: LineSegment StartX=-14.6 StartY=-11.85 StartZ=0 EndX=-9.6 EndY=-11.85 EndZ=0
    g6: LineSegment StartX=-19.6 StartY=-22.8 StartZ=0 EndX=-9.6 EndY=-22.8 EndZ=0
    g7: LineSegment StartX=-9.6 StartY=-11.85 StartZ=0 EndX=-9.6 EndY=-22.8 EndZ=0
  constraints (17):
    c: Coincident(g0,g-4)
    c: Coincident(g0,g-4)
    c: Coincident(g1,g0)
    c: Coincident(g1,g-3)
    c: Coincident(g2,g1)
    c: Coincident(g2,g-5)
    c: Coincident(g3,g2)
    c: Coincident(g3,g-7)
    c: Tangent(g4,g-7) = -1.5708
    c: Coincident(g4,g-8)
    c: Coincident(g5,g4)
    c: Coincident(g5,g-8)
    c: Coincident(g6,g0)
    c: Horizontal(g6)
    c: Coincident(g7,g5)
    c: Coincident(g6,g7)
    c: Vertical(g7)
FEATURE [PartDesign::Pad] Pad061
  BaseFeature = -> Pad060
  Direction = (-1e-15,-1,2e-16)
  Length = 2
  Length2 = 10
  Profile = -> Sketch102
  ReferenceAxis = -> Sketch102 [N_Axis]
  Refine = true
  Reversed = true
  Suppressed = false
  Type = 0
FEATURE [PartDesign::Body] Body002  label="Right_Leg"
  AllowCompound = false
  Group = -> [Binder001,Sketch082,Pad046,Sketch083,Pad047,Sketch084,Pocket037,Sketch085,Pad048,Sketch086,Pocket038,Sketch087,Pocket039,Fillet002,Sketch088,Pad049,Sketch089,Pocket040,Sketch090,Pad050,Sketch091,Pad051,Sketch092,Pad052,Sketch093,Pad053,Sketch094,Pad054,Sketch095,Pad055,Sketch096,Pocket041,Sketch097,Pad056,Sketch098,Pad057,Sketch099,Pad058,Sketch100,Pad059,Sketch101,Pad060,Sketch102,Pad061,+53 more]
  Origin = -> Origin002
  Placement = pos=(-31.1,0,-16.1) rot=(0,1,0;1.5708rad)
  Tip = -> Pocket182
